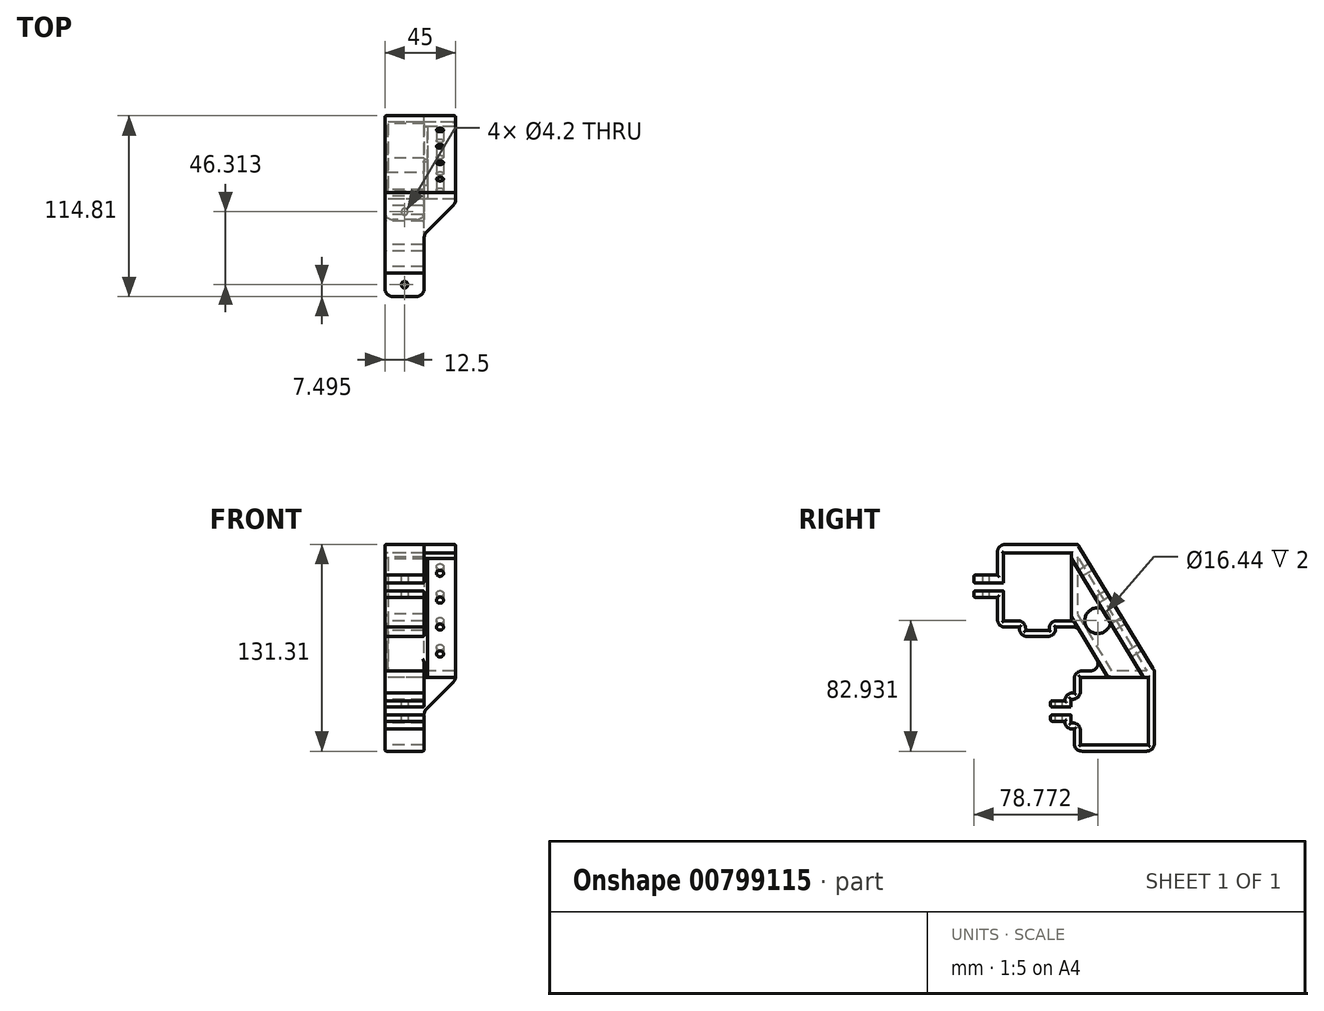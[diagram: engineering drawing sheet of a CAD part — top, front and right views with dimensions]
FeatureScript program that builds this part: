
annotation { "Feature Type Name" : "Feature", "Feature Type Description" : "" }
export const myFeature = defineFeature(function(context is Context, id is Id, definition is map)
    precondition{}
    {
        {
            var Q0;
            Q0=qCreatedBy(makeId("Right.planeOp"),FACE);
            var sketch = newSketch(context, id + "F0", { "sketchPlane" : qUnion([Q0])});
            skLineSegment(sketch, "E0.top", {"start": v(-257.11, -62.31) * mm, "end": v(-308.11, -62.31) * mm});
            skLineSegment(sketch, "E0.left", {"start": v(-257.11, -16.31) * mm, "end": v(-257.11, -62.31) * mm});
            skLineSegment(sketch, "E1.bottom", {"start": v(-304.11, -58.31) * mm, "end": v(-261.11, -58.31) * mm});
            skLineSegment(sketch, "E1.top", {"start": v(-304.11, -15.31) * mm, "end": v(-261.11, -15.31) * mm});
            skLineSegment(sketch, "E1.left", {"start": v(-304.11, -58.31) * mm, "end": v(-304.11, -44.31) * mm});
            skLineSegment(sketch, "E1.right", {"start": v(-261.11, -58.31) * mm, "end": v(-261.11, -15.31) * mm});
            skLineSegment(sketch, "E2.top", {"start": v(-323.11, -34.31) * mm, "end": v(-310.11, -34.31) * mm});
            skLineSegment(sketch, "E3.trimOffspring", {"start": v(-304.11, -29.31) * mm, "end": v(-304.11, -15.31) * mm});
            skLineSegment(sketch, "E4", {"start": v(-257.11, -11.31) * mm, "end": v(-308.11, -11.31) * mm});
            skLineSegment(sketch, "E5", {"start": v(-257.11, -16.31) * mm, "end": v(-257.11, -11.31) * mm});
            skLineSegment(sketch, "E6.top", {"start": v(-305.92, 16.5) * mm, "end": v(-323.92, 16.5) * mm});
            skLineSegment(sketch, "E6.left", {"start": v(-305.92, 64) * mm, "end": v(-305.92, 16.5) * mm});
            skLineSegment(sketch, "E7.bottom", {"start": v(-352.92, 20.5) * mm, "end": v(-338.92, 20.5) * mm});
            skLineSegment(sketch, "E7.top", {"start": v(-352.92, 63.5) * mm, "end": v(-309.92, 63.5) * mm});
            skLineSegment(sketch, "E7.left", {"start": v(-352.92, 20.5) * mm, "end": v(-352.92, 39.45) * mm});
            skLineSegment(sketch, "E7.right", {"start": v(-309.92, 20.5) * mm, "end": v(-309.92, 63.5) * mm});
            skLineSegment(sketch, "E8.top", {"start": v(-371.92, 44.5) * mm, "end": v(-352.92, 44.5) * mm});
            skLineSegment(sketch, "E9.trimOffspring", {"start": v(-352.92, 44.5) * mm, "end": v(-352.92, 63.5) * mm});
            skLineSegment(sketch, "E10", {"start": v(-356.92, 49.5) * mm, "end": v(-371.92, 49.5) * mm});
            skLineSegment(sketch, "E11", {"start": v(-371.92, 49.5) * mm, "end": v(-371.92, 44.5) * mm});
            skLineSegment(sketch, "E12", {"start": v(-305.92, 69) * mm, "end": v(-356.92, 69) * mm});
            skLineSegment(sketch, "E13", {"start": v(-305.92, 64) * mm, "end": v(-305.92, 69) * mm});
            skLineSegment(sketch, "E14", {"start": v(-305.92, 69) * mm, "end": v(-257.11, -11.31) * mm});
            skLineSegment(sketch, "E15", {"start": v(-305.92, 16.5) * mm, "end": v(-289.02, -11.31) * mm});
            skLineSegment(sketch, "E16", {"start": v(-266.47, -11.31) * mm, "end": v(-305.92, 53.6) * mm});
            skLineSegment(sketch, "E17", {"start": v(-289.02, -11.31) * mm, "end": v(-284.02, -11.31) * mm});
            skLineSegment(sketch, "E18", {"start": v(-284.02, -11.31) * mm, "end": v(-305.92, 24.73) * mm});
            skLineSegment(sketch, "E19", {"start": v(-276.96, 21.34) * mm, "end": v(-283.8, 17.19) * mm, "construction": true});
            skLineSegment(sketch, "E20", {"start": v(-309.92, 42) * mm, "end": v(-305.92, 42) * mm, "construction": true});
            skLineSegment(sketch, "E21", {"start": v(-261.11, -36.81) * mm, "end": v(-257.11, -36.81) * mm, "construction": true});
            skLineSegment(sketch, "E22", {"start": v(-331.42, 20.5) * mm, "end": v(-331.42, 16.5) * mm, "construction": true});
            skLineSegment(sketch, "E23", {"start": v(-332.38, 69) * mm, "end": v(-332.38, 63.5) * mm, "construction": true});
            skLineSegment(sketch, "E24", {"start": v(-356.92, 35.96) * mm, "end": v(-352.92, 35.96) * mm, "construction": true});
            skLineSegment(sketch, "E25", {"start": v(-356.92, 35.96) * mm, "end": v(-356.92, 16.5) * mm});
            skLineSegment(sketch, "E26", {"start": v(-352.92, 63.5) * mm, "end": v(-356.92, 63.5) * mm, "construction": true});
            skLineSegment(sketch, "E27", {"start": v(-356.92, 69) * mm, "end": v(-356.92, 49.5) * mm});
            skPoint(sketch, "E28.orphan", {"position": v(-358.83, 69) * mm});
            skLineSegment(sketch, "E29", {"start": v(-352.92, 39.45) * mm, "end": v(-371.92, 39.45) * mm});
            skLineSegment(sketch, "E30", {"start": v(-371.92, 39.45) * mm, "end": v(-371.92, 35.45) * mm});
            skLineSegment(sketch, "E31", {"start": v(-371.92, 35.45) * mm, "end": v(-356.92, 35.45) * mm});
            skLineSegment(sketch, "E32", {"start": v(-280.09, -58.31) * mm, "end": v(-280.09, -62.31) * mm, "construction": true});
            skLineSegment(sketch, "E33", {"start": v(-282.61, -15.31) * mm, "end": v(-282.61, -11.31) * mm, "construction": true});
            skLineSegment(sketch, "E34", {"start": v(-304.11, -15.31) * mm, "end": v(-308.11, -15.31) * mm, "construction": true});
            skLineSegment(sketch, "E35", {"start": v(-323.11, -34.31) * mm, "end": v(-323.11, -30.31) * mm});
            skLineSegment(sketch, "E36", {"start": v(-310.11, -30.31) * mm, "end": v(-323.11, -30.31) * mm});
            skLineSegment(sketch, "E37", {"start": v(-308.11, -25.31) * mm, "end": v(-308.11, -11.31) * mm});
            skLineSegment(sketch, "E38", {"start": v(-310.11, -39.31) * mm, "end": v(-323.11, -39.31) * mm});
            skLineSegment(sketch, "E39", {"start": v(-323.11, -39.31) * mm, "end": v(-323.11, -43.31) * mm});
            skLineSegment(sketch, "E40", {"start": v(-323.11, -43.31) * mm, "end": v(-310.11, -43.31) * mm});
            skLineSegment(sketch, "E41", {"start": v(-308.11, -48.31) * mm, "end": v(-308.11, -62.31) * mm});
            skLineSegment(sketch, "E42.bottom", {"start": v(-338.92, 14.5) * mm, "end": v(-323.92, 14.5) * mm});
            skLineSegment(sketch, "E42.left", {"start": v(-338.92, 14.5) * mm, "end": v(-338.92, 20.5) * mm});
            skLineSegment(sketch, "E42.right", {"start": v(-323.92, 14.5) * mm, "end": v(-323.92, 20.5) * mm});
            skPoint(sketch, "E42.middle", {"position": v(-331.42, 20.5) * mm});
            skLineSegment(sketch, "E43", {"start": v(-331.42, 14.5) * mm, "end": v(-331.42, 10.5) * mm, "construction": true});
            skLineSegment(sketch, "E44", {"start": v(-323.92, 15.67) * mm, "end": v(-319.92, 15.67) * mm, "construction": true});
            skLineSegment(sketch, "E45", {"start": v(-319.92, 16.5) * mm, "end": v(-319.92, 10.5) * mm});
            skLineSegment(sketch, "E46", {"start": v(-319.92, 10.5) * mm, "end": v(-331.42, 10.5) * mm});
            skLineSegment(sketch, "E47.MirrorCS", {"start": v(-342.92, 10.5) * mm, "end": v(-331.42, 10.5) * mm});
            skLineSegment(sketch, "E48.MirrorCS", {"start": v(-342.92, 16.5) * mm, "end": v(-342.92, 10.5) * mm});
            skPoint(sketch, "E49.orphan", {"position": v(-323.92, 26.5) * mm});
            skPoint(sketch, "E50.orphan", {"position": v(-338.92, 26.5) * mm});
            skLineSegment(sketch, "E51.trimOffspring", {"start": v(-323.92, 20.5) * mm, "end": v(-309.92, 20.5) * mm});
            skLineSegment(sketch, "E52.trimOffspring", {"start": v(-338.92, 16.5) * mm, "end": v(-356.92, 16.5) * mm});
            skLineSegment(sketch, "E53", {"start": v(-304.11, -34.31) * mm, "end": v(-304.11, -39.31) * mm, "construction": true});
            skLineSegment(sketch, "E54.bottom", {"start": v(-310.11, -44.31) * mm, "end": v(-304.11, -44.31) * mm});
            skLineSegment(sketch, "E54.top", {"start": v(-310.11, -29.31) * mm, "end": v(-304.11, -29.31) * mm});
            skLineSegment(sketch, "E54.left", {"start": v(-310.11, -44.31) * mm, "end": v(-310.11, -39.31) * mm});
            skPoint(sketch, "E54.middle", {"position": v(-304.11, -36.81) * mm});
            skLineSegment(sketch, "E55", {"start": v(-310.11, -29.31) * mm, "end": v(-310.11, -25.31) * mm, "construction": true});
            skLineSegment(sketch, "E56", {"start": v(-310.11, -29.31) * mm, "end": v(-314.11, -29.31) * mm, "construction": true});
            skLineSegment(sketch, "E57", {"start": v(-308.11, -25.31) * mm, "end": v(-314.11, -25.31) * mm});
            skLineSegment(sketch, "E58", {"start": v(-314.11, -25.31) * mm, "end": v(-314.11, -30.31) * mm});
            skLineSegment(sketch, "E59", {"start": v(-304.11, -36.81) * mm, "end": v(-328.83, -36.81) * mm, "construction": true});
            skLineSegment(sketch, "E60.MirrorCS", {"start": v(-314.11, -48.31) * mm, "end": v(-314.11, -43.31) * mm});
            skLineSegment(sketch, "E61.MirrorCS", {"start": v(-308.11, -48.31) * mm, "end": v(-314.11, -48.31) * mm});
            skLineSegment(sketch, "E62.trimOffspring", {"start": v(-310.11, -34.31) * mm, "end": v(-310.11, -29.31) * mm});
            skPoint(sketch, "E63.orphan", {"position": v(-298.11, -29.31) * mm});
            skPoint(sketch, "E64.orphan", {"position": v(-298.11, -44.31) * mm});
            skPoint(sketch, "E65.orphan", {"position": v(-308.11, -30.31) * mm});
            skPoint(sketch, "E66.orphan", {"position": v(-308.11, -43.31) * mm});
            skSolve(sketch);
        }
        {
            var Q0;
            Q0=qSketchRegion(id+"F0",true);
            extrude(context, id + "F1", {"entities" : qUnion([Q0]), "depth" : 25 * mm, "offsetDistance" : 25 * mm});
        }
        {
            var Q0;
            Q0=makeQuery(id+"F1.opExtrude","CAP_FACE",FACE,{"disambiguationData":[OSD([sQuery(id+"F0.wireOp",EDGE,"E0.top"),sQuery(id+"F0.wireOp",EDGE,"E0.left"),sQuery(id+"F0.wireOp",EDGE,"E1.bottom"),sQuery(id+"F0.wireOp",EDGE,"E1.top"),sQuery(id+"F0.wireOp",EDGE,"E1.left"),sQuery(id+"F0.wireOp",EDGE,"E1.right"),sQuery(id+"F0.wireOp",EDGE,"E2.bottom"),sQuery(id+"F0.wireOp",EDGE,"E2.top"),sQuery(id+"F0.wireOp",EDGE,"E3.trimOffspring"),sQuery(id+"F0.wireOp",EDGE,"97N35CGi-qyRt-fTuY-865t-gSXGTTs39KFh"),sQuery(id+"F0.wireOp",EDGE,"YVl5jyTW-9yZZ-gB00-PbPT-4uCPtmQBn0Fz"),sQuery(id+"F0.wireOp",EDGE,"DkqYmhQx-Zx2j-OynX-PNvr-HeUXXOLSZVF7"),sQuery(id+"F0.wireOp",EDGE,"8b463ff5-7117-4e72-8e2d-57af3a9758190.MirrorCS"),sQuery(id+"F0.wireOp",EDGE,"a2a913a1-f987-4361-a245-a8682805a7f70.MirrorCS"),sQuery(id+"F0.wireOp",EDGE,"813ea5ba-1d3b-4507-9dff-333e66d3a4c90.MirrorCS"),sQuery(id+"F0.wireOp",EDGE,"E4"),sQuery(id+"F0.wireOp",EDGE,"E5"),sQuery(id+"F0.wireOp",EDGE,"E6.top"),sQuery(id+"F0.wireOp",EDGE,"E6.left"),sQuery(id+"F0.wireOp",EDGE,"E7.bottom"),sQuery(id+"F0.wireOp",EDGE,"E7.top"),sQuery(id+"F0.wireOp",EDGE,"E7.left"),sQuery(id+"F0.wireOp",EDGE,"E7.right"),sQuery(id+"F0.wireOp",EDGE,"E8.bottom"),sQuery(id+"F0.wireOp",EDGE,"E8.top"),sQuery(id+"F0.wireOp",EDGE,"E9.trimOffspring"),sQuery(id+"F0.wireOp",EDGE,"463e9aad-9224-478d-ada1-befd63aa6510"),sQuery(id+"F0.wireOp",EDGE,"E10"),sQuery(id+"F0.wireOp",EDGE,"E11"),sQuery(id+"F0.wireOp",EDGE,"d85e5b7c-68ab-4a60-b65d-d2910f881e3b.MirrorCS"),sQuery(id+"F0.wireOp",EDGE,"648d8bc0-cce0-4394-85f9-bea9f80b14ba.MirrorCS"),sQuery(id+"F0.wireOp",EDGE,"03109c16-8484-40c6-ad21-c417801123f2.MirrorCS"),sQuery(id+"F0.wireOp",EDGE,"E12"),sQuery(id+"F0.wireOp",EDGE,"E14"),sQuery(id+"F0.wireOp",EDGE,"E15"),sQuery(id+"F0.wireOp",EDGE,"E16"),sQuery(id+"F0.wireOp",EDGE,"E18")])],"isStart":false});
            var sketch = newSketch(context, id + "F2", { "sketchPlane" : qUnion([Q0])});
            skLineSegment(sketch, "E67", {"start": v(-305.92, 69) * mm, "end": v(-257.11, -11.31) * mm});
            skLineSegment(sketch, "E68", {"start": v(-305.92, 53.6) * mm, "end": v(-263.95, -15.47) * mm});
            skLineSegment(sketch, "E69", {"start": v(-257.11, -11.31) * mm, "end": v(-263.95, -15.47) * mm});
            skLineSegment(sketch, "E70", {"start": v(-305.92, 69) * mm, "end": v(-312.76, 64.84) * mm});
            skLineSegment(sketch, "E71", {"start": v(-305.92, 53.6) * mm, "end": v(-313.8, 66.57) * mm});
            skLineSegment(sketch, "E72", {"start": v(-312.76, 64.84) * mm, "end": v(-313.8, 66.57) * mm});
            skPoint(sketch, "E73.orphan", {"position": v(-309.92, 66.57) * mm});
            skSolve(sketch);
        }
        {
            var Q0;
            Q0=qSketchRegion(id+"F2",true);
            extrude(context, id + "F3", {"entities" : qUnion([Q0]), "operationType" : NewBodyOperationType.ADD, "depth" : 20 * mm, "offsetDistance" : 25 * mm});
        }
        {
            var Q0;
            Q0=makeQuery(id+"F1.opExtrude","SWEPT_FACE",FACE,{"disambiguationData":[OSD([sQuery(id+"F0.wireOp",EDGE,"E40")])]});
            var sketch = newSketch(context, id + "F4", { "sketchPlane" : qUnion([Q0])});
            skCircle(sketch, "E74", {"center": v(12.5, 318.11) * mm, "radius": 2.1 * mm});
            skLineSegment(sketch, "E75", {"start": v(12.5, 318.11) * mm, "end": v(12.5, 323.11) * mm, "construction": true});
            skSolve(sketch);
        }
        {
            var Q0;
            Q0=qSketchRegion(id+"F4",true);
            extrude(context, id + "F5", {"entities" : qUnion([Q0]), "operationType" : NewBodyOperationType.REMOVE, "oppositeDirection" : true, "depth" : 25 * mm, "offsetDistance" : 25 * mm});
        }
        {
            var Q0;
            Q0=makeQuery(id+"F1.opExtrude","SWEPT_FACE",FACE,{"disambiguationData":[OSD([sQuery(id+"F0.wireOp",EDGE,"E31")])]});
            var sketch = newSketch(context, id + "F6", { "sketchPlane" : qUnion([Q0])});
            skLineSegment(sketch, "E76", {"start": v(0, 364.42) * mm, "end": v(25, 364.42) * mm, "construction": true});
            skCircle(sketch, "E77", {"center": v(12.5, 364.42) * mm, "radius": 2.1 * mm});
            skSolve(sketch);
        }
        {
            var Q0;
            Q0=qSketchRegion(id+"F6",true);
            extrude(context, id + "F7", {"entities" : qUnion([Q0]), "operationType" : NewBodyOperationType.REMOVE, "oppositeDirection" : true, "depth" : 25 * mm, "offsetDistance" : 25 * mm});
        }
        {
            var Q0;
            Q0=makeQuery(id+"F3.boolean.opBoolean","MERGE",FACE,{"derivedFrom":[makeQuery(id+"F1.opExtrude","SWEPT_FACE",FACE,{"disambiguationData":[OSD([sQuery(id+"F0.wireOp",EDGE,"E16")])]}),makeQuery(id+"F3.opExtrude","SWEPT_FACE",FACE,{"disambiguationData":[OSD([sQuery(id+"F2.wireOp",EDGE,"E68"),sQuery(id+"F2.wireOp",EDGE,"E71")])]})]});
            var sketch = newSketch(context, id + "F8", { "sketchPlane" : qUnion([Q0])});
            skLineSegment(sketch, "E78", {"start": v(35, 124.76) * mm, "end": v(35, 217.85) * mm, "construction": true});
            skPoint(sketch, "E78.startSnap0", {"position": v(35, 123.87) * mm});
            skLineSegment(sketch, "E79", {"start": v(35, 171.3) * mm, "end": v(25.9, 171.3) * mm, "construction": true});
            skLineSegment(sketch, "E80", {"start": v(25.9, 171.3) * mm, "end": v(45, 171.3) * mm, "construction": true});
            skLineSegment(sketch, "E81", {"start": v(35, 171.3) * mm, "end": v(35, 181.3) * mm, "construction": true});
            skLineSegment(sketch, "E82", {"start": v(35, 181.3) * mm, "end": v(35, 201.3) * mm, "construction": true});
            skCircle(sketch, "E83", {"center": v(35, 181.3) * mm, "radius": 2.25 * mm});
            skCircle(sketch, "E84", {"center": v(35, 201.3) * mm, "radius": 2.25 * mm});
            skCircle(sketch, "E85.MirrorC", {"center": v(35, 161.3) * mm, "radius": 2.25 * mm});
            skCircle(sketch, "E86.MirrorC", {"center": v(35, 141.3) * mm, "radius": 2.25 * mm});
            skSolve(sketch);
        }
        {
            var Q0;
            Q0=qSketchRegion(id+"F8",true);
            extrude(context, id + "F9", {"entities" : qUnion([Q0]), "operationType" : NewBodyOperationType.REMOVE, "oppositeDirection" : true, "depth" : 25 * mm, "offsetDistance" : 25 * mm});
        }
        {
            var Q0;
            {var subQ0=sQuery(id+"F0.wireOp",EDGE,"E27");var subQ5=sQuery(id+"F0.wireOp",EDGE,"E16");var subQ6=sQuery(id+"F0.wireOp",EDGE,"E14");var subQ7=sQuery(id+"F0.wireOp",EDGE,"E12");var subQ8=sQuery(id+"F0.wireOp",EDGE,"E11");var subQ9=sQuery(id+"F0.wireOp",EDGE,"E7.top");var subQ10=sQuery(id+"F0.wireOp",EDGE,"E10");var subQ11=sQuery(id+"F0.wireOp",EDGE,"E8.top");var subQ12=sQuery(id+"F0.wireOp",EDGE,"E9.trimOffspring");Q0=makeQuery(id+"F3.boolean.opBoolean","SPLIT",FACE,{"disambiguationData":[TD([makeQuery(id+"F1.opExtrude","SWEPT_FACE",FACE,{"disambiguationData":[OSD([subQ9])]})])],"derivedFrom":makeQuery(id+"F1.opExtrude","CAP_FACE",FACE,{"disambiguationData":[OSD([sQuery(id+"F0.wireOp",EDGE,"E0.top"),sQuery(id+"F0.wireOp",EDGE,"E0.left"),sQuery(id+"F0.wireOp",EDGE,"E1.bottom"),sQuery(id+"F0.wireOp",EDGE,"E1.top"),sQuery(id+"F0.wireOp",EDGE,"E1.left"),sQuery(id+"F0.wireOp",EDGE,"E1.right"),sQuery(id+"F0.wireOp",EDGE,"E2.top"),sQuery(id+"F0.wireOp",EDGE,"E3.trimOffspring"),sQuery(id+"F0.wireOp",EDGE,"E4"),sQuery(id+"F0.wireOp",EDGE,"E5"),sQuery(id+"F0.wireOp",EDGE,"E6.top"),sQuery(id+"F0.wireOp",EDGE,"E6.left"),sQuery(id+"F0.wireOp",EDGE,"E7.bottom"),subQ9,sQuery(id+"F0.wireOp",EDGE,"E7.left"),sQuery(id+"F0.wireOp",EDGE,"E7.right"),subQ11,subQ12,subQ10,subQ8,subQ7,subQ6,sQuery(id+"F0.wireOp",EDGE,"E15"),subQ5,sQuery(id+"F0.wireOp",EDGE,"E18"),sQuery(id+"F0.wireOp",EDGE,"E25"),subQ0,sQuery(id+"F0.wireOp",EDGE,"E29"),sQuery(id+"F0.wireOp",EDGE,"E30"),sQuery(id+"F0.wireOp",EDGE,"E31"),sQuery(id+"F0.wireOp",EDGE,"E35"),sQuery(id+"F0.wireOp",EDGE,"E36"),sQuery(id+"F0.wireOp",EDGE,"E37"),sQuery(id+"F0.wireOp",EDGE,"E38"),sQuery(id+"F0.wireOp",EDGE,"E39"),sQuery(id+"F0.wireOp",EDGE,"E40"),sQuery(id+"F0.wireOp",EDGE,"E41"),sQuery(id+"F0.wireOp",EDGE,"E42.bottom"),sQuery(id+"F0.wireOp",EDGE,"E42.left"),sQuery(id+"F0.wireOp",EDGE,"E42.right"),sQuery(id+"F0.wireOp",EDGE,"E45"),sQuery(id+"F0.wireOp",EDGE,"E46"),sQuery(id+"F0.wireOp",EDGE,"E47.MirrorCS"),sQuery(id+"F0.wireOp",EDGE,"E48.MirrorCS"),sQuery(id+"F0.wireOp",EDGE,"E51.trimOffspring"),sQuery(id+"F0.wireOp",EDGE,"E52.trimOffspring"),sQuery(id+"F0.wireOp",EDGE,"E54.bottom"),sQuery(id+"F0.wireOp",EDGE,"E54.top"),sQuery(id+"F0.wireOp",EDGE,"E54.left"),sQuery(id+"F0.wireOp",EDGE,"E57"),sQuery(id+"F0.wireOp",EDGE,"E58"),sQuery(id+"F0.wireOp",EDGE,"E60.MirrorCS"),sQuery(id+"F0.wireOp",EDGE,"E61.MirrorCS"),sQuery(id+"F0.wireOp",EDGE,"E62.trimOffspring")])],"isStart":false})});}
            var sketch = newSketch(context, id + "F10", { "sketchPlane" : qUnion([Q0])});
            skLineSegment(sketch, "E87.bottom", {"start": v(-284.02, -11.31) * mm, "end": v(-284.02, -11.31) * mm});
            skLineSegment(sketch, "E87.top", {"start": v(-284.02, -15.31) * mm, "end": v(-284.02, -15.31) * mm});
            skLineSegment(sketch, "E87.left", {"start": v(-284.02, -11.31) * mm, "end": v(-284.02, -15.31) * mm});
            skLineSegment(sketch, "E87.right", {"start": v(-284.02, -11.31) * mm, "end": v(-284.02, -15.31) * mm});
            skLineSegment(sketch, "E88.bottom", {"start": v(-332.43, 63.5) * mm, "end": v(-305.92, 63.5) * mm});
            skLineSegment(sketch, "E88.top", {"start": v(-332.43, 69) * mm, "end": v(-305.92, 69) * mm});
            skLineSegment(sketch, "E88.left", {"start": v(-332.43, 63.5) * mm, "end": v(-332.43, 69) * mm});
            skLineSegment(sketch, "E88.right", {"start": v(-305.92, 63.5) * mm, "end": v(-305.92, 69) * mm});
            skSolve(sketch);
        }
        {
            var Q0;
            Q0=qSketchRegion(id+"F10",true);
            extrude(context, id + "F11", {"entities" : qUnion([Q0]), "operationType" : NewBodyOperationType.ADD, "depth" : 20 * mm, "offsetDistance" : 25 * mm});
        }
        {
            var Q0;
            {var subQ0=sQuery(id+"F0.wireOp",EDGE,"E38");var subQ1=sQuery(id+"F0.wireOp",EDGE,"E14");var subQ2=sQuery(id+"F0.wireOp",EDGE,"E0.top");var subQ3=sQuery(id+"F0.wireOp",EDGE,"E1.right");var subQ4=sQuery(id+"F0.wireOp",EDGE,"E61.MirrorCS");var subQ5=sQuery(id+"F0.wireOp",EDGE,"E1.left");var subQ6=sQuery(id+"F0.wireOp",EDGE,"E60.MirrorCS");var subQ7=sQuery(id+"F0.wireOp",EDGE,"E1.top");var subQ10=sQuery(id+"F0.wireOp",EDGE,"E39");var subQ11=sQuery(id+"F0.wireOp",EDGE,"E5");var subQ12=sQuery(id+"F0.wireOp",EDGE,"E0.left");var subQ13=sQuery(id+"F0.wireOp",EDGE,"E54.left");var subQ14=sQuery(id+"F0.wireOp",EDGE,"E40");var subQ15=sQuery(id+"F0.wireOp",EDGE,"E1.bottom");var subQ16=sQuery(id+"F0.wireOp",EDGE,"E41");var subQ17=sQuery(id+"F0.wireOp",EDGE,"E54.bottom");Q0=makeQuery(id+"F3.boolean.opBoolean","SPLIT",FACE,{"disambiguationData":[TD([makeQuery(id+"F1.opExtrude","SWEPT_FACE",FACE,{"disambiguationData":[OSD([subQ2])]})])],"derivedFrom":makeQuery(id+"F1.opExtrude","CAP_FACE",FACE,{"disambiguationData":[OSD([subQ2,subQ12,subQ15,subQ7,subQ5,subQ3,sQuery(id+"F0.wireOp",EDGE,"E2.top"),sQuery(id+"F0.wireOp",EDGE,"E3.trimOffspring"),sQuery(id+"F0.wireOp",EDGE,"E4"),subQ11,sQuery(id+"F0.wireOp",EDGE,"E6.top"),sQuery(id+"F0.wireOp",EDGE,"E6.left"),sQuery(id+"F0.wireOp",EDGE,"E7.bottom"),sQuery(id+"F0.wireOp",EDGE,"E7.top"),sQuery(id+"F0.wireOp",EDGE,"E7.left"),sQuery(id+"F0.wireOp",EDGE,"E7.right"),sQuery(id+"F0.wireOp",EDGE,"E8.top"),sQuery(id+"F0.wireOp",EDGE,"E9.trimOffspring"),sQuery(id+"F0.wireOp",EDGE,"E10"),sQuery(id+"F0.wireOp",EDGE,"E11"),sQuery(id+"F0.wireOp",EDGE,"E12"),subQ1,sQuery(id+"F0.wireOp",EDGE,"E15"),sQuery(id+"F0.wireOp",EDGE,"E16"),sQuery(id+"F0.wireOp",EDGE,"E18"),sQuery(id+"F0.wireOp",EDGE,"E25"),sQuery(id+"F0.wireOp",EDGE,"E27"),sQuery(id+"F0.wireOp",EDGE,"E29"),sQuery(id+"F0.wireOp",EDGE,"E30"),sQuery(id+"F0.wireOp",EDGE,"E31"),sQuery(id+"F0.wireOp",EDGE,"E35"),sQuery(id+"F0.wireOp",EDGE,"E36"),sQuery(id+"F0.wireOp",EDGE,"E37"),subQ0,subQ10,subQ14,subQ16,sQuery(id+"F0.wireOp",EDGE,"E42.bottom"),sQuery(id+"F0.wireOp",EDGE,"E42.left"),sQuery(id+"F0.wireOp",EDGE,"E42.right"),sQuery(id+"F0.wireOp",EDGE,"E45"),sQuery(id+"F0.wireOp",EDGE,"E46"),sQuery(id+"F0.wireOp",EDGE,"E47.MirrorCS"),sQuery(id+"F0.wireOp",EDGE,"E48.MirrorCS"),sQuery(id+"F0.wireOp",EDGE,"E51.trimOffspring"),sQuery(id+"F0.wireOp",EDGE,"E52.trimOffspring"),subQ17,sQuery(id+"F0.wireOp",EDGE,"E54.top"),subQ13,sQuery(id+"F0.wireOp",EDGE,"E57"),sQuery(id+"F0.wireOp",EDGE,"E58"),subQ6,subQ4,sQuery(id+"F0.wireOp",EDGE,"E62.trimOffspring")])],"isStart":false})});}
            var sketch = newSketch(context, id + "F12", { "sketchPlane" : qUnion([Q0])});
            skLineSegment(sketch, "E89.bottom", {"start": v(-257.11, -36.81) * mm, "end": v(-261.11, -36.81) * mm});
            skLineSegment(sketch, "E89.top", {"start": v(-257.11, -11.31) * mm, "end": v(-261.11, -11.31) * mm});
            skLineSegment(sketch, "E89.left", {"start": v(-257.11, -36.81) * mm, "end": v(-257.11, -11.31) * mm});
            skLineSegment(sketch, "E89.right", {"start": v(-261.11, -36.81) * mm, "end": v(-261.11, -11.31) * mm});
            skSolve(sketch);
        }
        {
            var Q0;
            Q0=qSketchRegion(id+"F12",true);
            extrude(context, id + "F13", {"entities" : qUnion([Q0]), "operationType" : NewBodyOperationType.ADD, "depth" : 20 * mm, "offsetDistance" : 25 * mm});
        }
        {
            var Q0;
            {var subQ0=sQuery(id+"F0.wireOp",EDGE,"E30");var subQ1=sQuery(id+"F0.wireOp",EDGE,"E29");var subQ4=sQuery(id+"F0.wireOp",EDGE,"E25");var subQ5=sQuery(id+"F0.wireOp",EDGE,"E18");var subQ6=sQuery(id+"F0.wireOp",EDGE,"E16");var subQ7=sQuery(id+"F0.wireOp",EDGE,"E15");var subQ8=sQuery(id+"F0.wireOp",EDGE,"E35");var subQ9=sQuery(id+"F0.wireOp",EDGE,"E3.trimOffspring");var subQ10=sQuery(id+"F0.wireOp",EDGE,"E31");var subQ11=sQuery(id+"F0.wireOp",EDGE,"E2.top");var subQ12=sQuery(id+"F0.wireOp",EDGE,"E36");var subQ13=sQuery(id+"F0.wireOp",EDGE,"E4");var subQ15=sQuery(id+"F0.wireOp",EDGE,"E1.top");var subQ16=sQuery(id+"F0.wireOp",EDGE,"E42.bottom");var subQ17=sQuery(id+"F0.wireOp",EDGE,"E7.left");var subQ18=sQuery(id+"F0.wireOp",EDGE,"E37");var subQ19=sQuery(id+"F0.wireOp",EDGE,"E6.top");var subQ20=sQuery(id+"F0.wireOp",EDGE,"E6.left");var subQ21=sQuery(id+"F0.wireOp",EDGE,"E7.bottom");var subQ22=sQuery(id+"F0.wireOp",EDGE,"E42.left");var subQ23=sQuery(id+"F0.wireOp",EDGE,"E7.right");var subQ24=sQuery(id+"F0.wireOp",EDGE,"E42.right");var subQ25=sQuery(id+"F0.wireOp",EDGE,"E45");var subQ26=sQuery(id+"F0.wireOp",EDGE,"E47.MirrorCS");var subQ27=sQuery(id+"F0.wireOp",EDGE,"E46");var subQ28=sQuery(id+"F0.wireOp",EDGE,"E48.MirrorCS");var subQ29=sQuery(id+"F0.wireOp",EDGE,"E51.trimOffspring");var subQ30=sQuery(id+"F0.wireOp",EDGE,"E52.trimOffspring");var subQ31=sQuery(id+"F0.wireOp",EDGE,"E54.top");var subQ32=sQuery(id+"F0.wireOp",EDGE,"E57");var subQ33=sQuery(id+"F0.wireOp",EDGE,"E58");var subQ34=sQuery(id+"F0.wireOp",EDGE,"E62.trimOffspring");Q0=makeQuery(id+"F3.boolean.opBoolean","SPLIT",FACE,{"disambiguationData":[TD([makeQuery(id+"F1.opExtrude","SWEPT_FACE",FACE,{"disambiguationData":[OSD([subQ11])]})])],"derivedFrom":makeQuery(id+"F1.opExtrude","CAP_FACE",FACE,{"disambiguationData":[OSD([sQuery(id+"F0.wireOp",EDGE,"E0.top"),sQuery(id+"F0.wireOp",EDGE,"E0.left"),sQuery(id+"F0.wireOp",EDGE,"E1.bottom"),subQ15,sQuery(id+"F0.wireOp",EDGE,"E1.left"),sQuery(id+"F0.wireOp",EDGE,"E1.right"),subQ11,subQ9,subQ13,sQuery(id+"F0.wireOp",EDGE,"E5"),subQ19,subQ20,subQ21,sQuery(id+"F0.wireOp",EDGE,"E7.top"),subQ17,subQ23,sQuery(id+"F0.wireOp",EDGE,"E8.top"),sQuery(id+"F0.wireOp",EDGE,"E9.trimOffspring"),sQuery(id+"F0.wireOp",EDGE,"E10"),sQuery(id+"F0.wireOp",EDGE,"E11"),sQuery(id+"F0.wireOp",EDGE,"E12"),sQuery(id+"F0.wireOp",EDGE,"E14"),subQ7,subQ6,subQ5,subQ4,sQuery(id+"F0.wireOp",EDGE,"E27"),subQ1,subQ0,subQ10,subQ8,subQ12,subQ18,sQuery(id+"F0.wireOp",EDGE,"E38"),sQuery(id+"F0.wireOp",EDGE,"E39"),sQuery(id+"F0.wireOp",EDGE,"E40"),sQuery(id+"F0.wireOp",EDGE,"E41"),subQ16,subQ22,subQ24,subQ25,subQ27,subQ26,subQ28,subQ29,subQ30,sQuery(id+"F0.wireOp",EDGE,"E54.bottom"),subQ31,sQuery(id+"F0.wireOp",EDGE,"E54.left"),subQ32,subQ33,sQuery(id+"F0.wireOp",EDGE,"E60.MirrorCS"),sQuery(id+"F0.wireOp",EDGE,"E61.MirrorCS"),subQ34])],"isStart":false})});}
            var sketch = newSketch(context, id + "F14", { "sketchPlane" : qUnion([Q0])});
            skLineSegment(sketch, "E90.bottom", {"start": v(-264.04, -15.31) * mm, "end": v(-259.49, -15.31) * mm});
            skLineSegment(sketch, "E90.top", {"start": v(-264.04, -12.49) * mm, "end": v(-259.49, -12.49) * mm});
            skLineSegment(sketch, "E90.left", {"start": v(-264.04, -15.31) * mm, "end": v(-264.04, -12.49) * mm});
            skLineSegment(sketch, "E90.right", {"start": v(-259.49, -15.31) * mm, "end": v(-259.49, -12.49) * mm});
            skSolve(sketch);
        }
        {
            var Q0;
            Q0=qSketchRegion(id+"F14",true);
            extrude(context, id + "F15", {"entities" : qUnion([Q0]), "operationType" : NewBodyOperationType.ADD, "depth" : 20 * mm, "offsetDistance" : 25 * mm});
        }
        {
            var Q0;
            {var subQ1=sQuery(id+"F0.wireOp",EDGE,"E7.top");var subQ2=sQuery(id+"F2.wireOp",EDGE,"E71");var subQ3=sQuery(id+"F2.wireOp",EDGE,"E68");Q0=makeQuery(id+"F3.boolean.opBoolean","SPLIT",FACE,{"disambiguationData":[TD([makeQuery(id+"F1.opExtrude","SWEPT_FACE",FACE,{"disambiguationData":[OSD([subQ1])]})])],"derivedFrom":makeQuery(id+"F3.opExtrude","CAP_FACE",FACE,{"disambiguationData":[OSD([sQuery(id+"F2.wireOp",EDGE,"E67"),subQ3,sQuery(id+"F2.wireOp",EDGE,"E69"),sQuery(id+"F2.wireOp",EDGE,"E70"),subQ2])],"isStart":true})});}
            var sketch = newSketch(context, id + "F16", { "sketchPlane" : qUnion([Q0])});
            skLineSegment(sketch, "E91", {"start": v(309.92, 63.5) * mm, "end": v(309.92, 60.18) * mm});
            skLineSegment(sketch, "E92", {"start": v(309.92, 60.18) * mm, "end": v(311.94, 63.5) * mm});
            skLineSegment(sketch, "E93", {"start": v(311.94, 63.5) * mm, "end": v(309.92, 63.5) * mm});
            skSolve(sketch);
        }
        {
            var Q0;
            Q0=qSketchRegion(id+"F16",true);
            extrude(context, id + "F17", {"entities" : qUnion([Q0]), "operationType" : NewBodyOperationType.REMOVE, "oppositeDirection" : true, "depth" : 20 * mm, "offsetDistance" : 25 * mm});
        }
        {
            var Q0;
            Q0=makeQuery(id+"F13.opExtrude","CAP_EDGE",EDGE,{"disambiguationData":[OSD([sQuery(id+"F12.wireOp",EDGE,"E89.bottom")])],"isStart":false});
            var Q1;
            Q1=makeQuery(id+"F11.opExtrude","CAP_EDGE",EDGE,{"disambiguationData":[OSD([sQuery(id+"F10.wireOp",EDGE,"E88.left")])],"isStart":false});
            chamfer(context, id + "F18", {"entities" : qUnion([Q0, Q1]), "width" : 20 * mm, "tangentPropagation" : true});
        }
        {
            var Q0;
            {var subQ0=sQuery(id+"F0.wireOp",EDGE,"E30");var subQ1=sQuery(id+"F0.wireOp",EDGE,"E29");var subQ4=sQuery(id+"F0.wireOp",EDGE,"E25");var subQ5=sQuery(id+"F0.wireOp",EDGE,"E18");var subQ6=sQuery(id+"F0.wireOp",EDGE,"E16");var subQ7=sQuery(id+"F0.wireOp",EDGE,"E15");var subQ8=sQuery(id+"F0.wireOp",EDGE,"E35");var subQ9=sQuery(id+"F0.wireOp",EDGE,"E3.trimOffspring");var subQ10=sQuery(id+"F0.wireOp",EDGE,"E31");var subQ11=sQuery(id+"F0.wireOp",EDGE,"E2.top");var subQ12=sQuery(id+"F0.wireOp",EDGE,"E36");var subQ13=sQuery(id+"F0.wireOp",EDGE,"E4");var subQ15=sQuery(id+"F0.wireOp",EDGE,"E1.top");var subQ16=sQuery(id+"F0.wireOp",EDGE,"E42.bottom");var subQ17=sQuery(id+"F0.wireOp",EDGE,"E7.left");var subQ18=sQuery(id+"F0.wireOp",EDGE,"E37");var subQ19=sQuery(id+"F0.wireOp",EDGE,"E6.top");var subQ20=sQuery(id+"F0.wireOp",EDGE,"E6.left");var subQ21=sQuery(id+"F0.wireOp",EDGE,"E7.bottom");var subQ22=sQuery(id+"F0.wireOp",EDGE,"E42.left");var subQ23=sQuery(id+"F0.wireOp",EDGE,"E7.right");var subQ24=sQuery(id+"F0.wireOp",EDGE,"E42.right");var subQ25=sQuery(id+"F0.wireOp",EDGE,"E45");var subQ26=sQuery(id+"F0.wireOp",EDGE,"E47.MirrorCS");var subQ27=sQuery(id+"F0.wireOp",EDGE,"E46");var subQ28=sQuery(id+"F0.wireOp",EDGE,"E48.MirrorCS");var subQ29=sQuery(id+"F0.wireOp",EDGE,"E51.trimOffspring");var subQ30=sQuery(id+"F0.wireOp",EDGE,"E52.trimOffspring");var subQ31=sQuery(id+"F0.wireOp",EDGE,"E54.top");var subQ32=sQuery(id+"F0.wireOp",EDGE,"E57");var subQ33=sQuery(id+"F0.wireOp",EDGE,"E58");var subQ34=sQuery(id+"F0.wireOp",EDGE,"E62.trimOffspring");Q0=makeQuery(id+"F3.boolean.opBoolean","SPLIT",FACE,{"disambiguationData":[TD([makeQuery(id+"F1.opExtrude","SWEPT_FACE",FACE,{"disambiguationData":[OSD([subQ11])]})])],"derivedFrom":makeQuery(id+"F1.opExtrude","CAP_FACE",FACE,{"disambiguationData":[OSD([sQuery(id+"F0.wireOp",EDGE,"E0.top"),sQuery(id+"F0.wireOp",EDGE,"E0.left"),sQuery(id+"F0.wireOp",EDGE,"E1.bottom"),subQ15,sQuery(id+"F0.wireOp",EDGE,"E1.left"),sQuery(id+"F0.wireOp",EDGE,"E1.right"),subQ11,subQ9,subQ13,sQuery(id+"F0.wireOp",EDGE,"E5"),subQ19,subQ20,subQ21,sQuery(id+"F0.wireOp",EDGE,"E7.top"),subQ17,subQ23,sQuery(id+"F0.wireOp",EDGE,"E8.top"),sQuery(id+"F0.wireOp",EDGE,"E9.trimOffspring"),sQuery(id+"F0.wireOp",EDGE,"E10"),sQuery(id+"F0.wireOp",EDGE,"E11"),sQuery(id+"F0.wireOp",EDGE,"E12"),sQuery(id+"F0.wireOp",EDGE,"E14"),subQ7,subQ6,subQ5,subQ4,sQuery(id+"F0.wireOp",EDGE,"E27"),subQ1,subQ0,subQ10,subQ8,subQ12,subQ18,sQuery(id+"F0.wireOp",EDGE,"E38"),sQuery(id+"F0.wireOp",EDGE,"E39"),sQuery(id+"F0.wireOp",EDGE,"E40"),sQuery(id+"F0.wireOp",EDGE,"E41"),subQ16,subQ22,subQ24,subQ25,subQ27,subQ26,subQ28,subQ29,subQ30,sQuery(id+"F0.wireOp",EDGE,"E54.bottom"),subQ31,sQuery(id+"F0.wireOp",EDGE,"E54.left"),subQ32,subQ33,sQuery(id+"F0.wireOp",EDGE,"E60.MirrorCS"),sQuery(id+"F0.wireOp",EDGE,"E61.MirrorCS"),subQ34])],"isStart":false})});}
            var sketch = newSketch(context, id + "F19", { "sketchPlane" : qUnion([Q0])});
            skLineSegment(sketch, "E94", {"start": v(-264.04, -15.31) * mm, "end": v(-309.92, 60.18) * mm});
            skLineSegment(sketch, "E95", {"start": v(-289.02, -11.31) * mm, "end": v(-309.92, 23.08) * mm});
            skLineSegment(sketch, "E96", {"start": v(-309.92, 23.08) * mm, "end": v(-309.92, 60.18) * mm});
            skLineSegment(sketch, "E97", {"start": v(-289.02, -11.31) * mm, "end": v(-286.59, -15.31) * mm});
            skLineSegment(sketch, "E98", {"start": v(-286.59, -15.31) * mm, "end": v(-264.04, -15.31) * mm});
            skSolve(sketch);
        }
        {
            var Q0;
            Q0=qSketchRegion(id+"F19",true);
            extrude(context, id + "F20", {"entities" : qUnion([Q0]), "operationType" : NewBodyOperationType.ADD, "depth" : 2 * mm, "offsetDistance" : 25 * mm});
        }
        {
            var Q0;
            Q0=makeQuery(id+"F1.opExtrude","CAP_FACE",FACE,{"disambiguationData":[OSD([sQuery(id+"F0.wireOp",EDGE,"E0.top"),sQuery(id+"F0.wireOp",EDGE,"E0.left"),sQuery(id+"F0.wireOp",EDGE,"E1.bottom"),sQuery(id+"F0.wireOp",EDGE,"E1.top"),sQuery(id+"F0.wireOp",EDGE,"E1.left"),sQuery(id+"F0.wireOp",EDGE,"E1.right"),sQuery(id+"F0.wireOp",EDGE,"E2.top"),sQuery(id+"F0.wireOp",EDGE,"E3.trimOffspring"),sQuery(id+"F0.wireOp",EDGE,"E4"),sQuery(id+"F0.wireOp",EDGE,"E5"),sQuery(id+"F0.wireOp",EDGE,"E6.top"),sQuery(id+"F0.wireOp",EDGE,"E6.left"),sQuery(id+"F0.wireOp",EDGE,"E7.bottom"),sQuery(id+"F0.wireOp",EDGE,"E7.top"),sQuery(id+"F0.wireOp",EDGE,"E7.left"),sQuery(id+"F0.wireOp",EDGE,"E7.right"),sQuery(id+"F0.wireOp",EDGE,"E8.top"),sQuery(id+"F0.wireOp",EDGE,"E9.trimOffspring"),sQuery(id+"F0.wireOp",EDGE,"E10"),sQuery(id+"F0.wireOp",EDGE,"E11"),sQuery(id+"F0.wireOp",EDGE,"E12"),sQuery(id+"F0.wireOp",EDGE,"E14"),sQuery(id+"F0.wireOp",EDGE,"E15"),sQuery(id+"F0.wireOp",EDGE,"E16"),sQuery(id+"F0.wireOp",EDGE,"E18"),sQuery(id+"F0.wireOp",EDGE,"E25"),sQuery(id+"F0.wireOp",EDGE,"E27"),sQuery(id+"F0.wireOp",EDGE,"E29"),sQuery(id+"F0.wireOp",EDGE,"E30"),sQuery(id+"F0.wireOp",EDGE,"E31"),sQuery(id+"F0.wireOp",EDGE,"E35"),sQuery(id+"F0.wireOp",EDGE,"E36"),sQuery(id+"F0.wireOp",EDGE,"E37"),sQuery(id+"F0.wireOp",EDGE,"E38"),sQuery(id+"F0.wireOp",EDGE,"E39"),sQuery(id+"F0.wireOp",EDGE,"E40"),sQuery(id+"F0.wireOp",EDGE,"E41"),sQuery(id+"F0.wireOp",EDGE,"E42.bottom"),sQuery(id+"F0.wireOp",EDGE,"E42.left"),sQuery(id+"F0.wireOp",EDGE,"E42.right"),sQuery(id+"F0.wireOp",EDGE,"E45"),sQuery(id+"F0.wireOp",EDGE,"E46"),sQuery(id+"F0.wireOp",EDGE,"E47.MirrorCS"),sQuery(id+"F0.wireOp",EDGE,"E48.MirrorCS"),sQuery(id+"F0.wireOp",EDGE,"E51.trimOffspring"),sQuery(id+"F0.wireOp",EDGE,"E52.trimOffspring"),sQuery(id+"F0.wireOp",EDGE,"E54.bottom"),sQuery(id+"F0.wireOp",EDGE,"E54.top"),sQuery(id+"F0.wireOp",EDGE,"E54.left"),sQuery(id+"F0.wireOp",EDGE,"E57"),sQuery(id+"F0.wireOp",EDGE,"E58"),sQuery(id+"F0.wireOp",EDGE,"E60.MirrorCS"),sQuery(id+"F0.wireOp",EDGE,"E61.MirrorCS"),sQuery(id+"F0.wireOp",EDGE,"E62.trimOffspring")])],"isStart":true});
            var sketch = newSketch(context, id + "F21", { "sketchPlane" : qUnion([Q0])});
            skLineSegment(sketch, "E99", {"start": v(266.47, -11.31) * mm, "end": v(262, -11.31) * mm});
            skLineSegment(sketch, "E100", {"start": v(262, -11.31) * mm, "end": v(305.19, 59.73) * mm});
            skLineSegment(sketch, "E101", {"start": v(305.92, 53.6) * mm, "end": v(266.47, -11.31) * mm});
            skLineSegment(sketch, "E102", {"start": v(305.92, 53.6) * mm, "end": v(305.92, 61.01) * mm});
            skLineSegment(sketch, "E103", {"start": v(305.92, 61.01) * mm, "end": v(305.19, 59.73) * mm});
            skSolve(sketch);
        }
        {
            var Q0;
            Q0=makeQuery(id+"F21.imprint","IMPRINT",FACE,{"disambiguationData":[TD([[makeQuery(id+"F21.imprint","IMPRINT",EDGE,{"derivedFrom":sQuery(id+"F21.wireOp",EDGE,"E99")}),-1.0]])]});
            extrude(context, id + "F22", {"entities" : qUnion([Q0]), "operationType" : NewBodyOperationType.REMOVE, "oppositeDirection" : true, "depth" : 25 * mm, "offsetDistance" : 25 * mm});
        }
        {
            var Q0;
            Q0=makeQuery(id+"F22.boolean.opBoolean","MERGE",FACE,{"derivedFrom":[makeQuery(id+"F20.opExtrude","CAP_FACE",FACE,{"disambiguationData":[OSD([sQuery(id+"F19.wireOp",EDGE,"E94"),sQuery(id+"F19.wireOp",EDGE,"E95"),sQuery(id+"F19.wireOp",EDGE,"E96"),sQuery(id+"F19.wireOp",EDGE,"E97"),sQuery(id+"F19.wireOp",EDGE,"E98")])],"isStart":true})],"fromTools":[makeQuery(id+"F22.opExtrude","CAP_FACE",FACE,{"disambiguationData":[OSD([sQuery(id+"F21.wireOp",EDGE,"E99"),sQuery(id+"F21.wireOp",EDGE,"E100"),sQuery(id+"F21.wireOp",EDGE,"E101"),sQuery(id+"F21.wireOp",EDGE,"E102"),sQuery(id+"F21.wireOp",EDGE,"E103")])],"isStart":false})]});
            var sketch = newSketch(context, id + "F23", { "sketchPlane" : qUnion([Q0])});
            skCircle(sketch, "E104", {"center": v(293.15, 20.62) * mm, "radius": 8.22 * mm});
            skSolve(sketch);
        }
        {
            var Q0;
            Q0=qSketchRegion(id+"F23",true);
            extrude(context, id + "F24", {"entities" : qUnion([Q0]), "operationType" : NewBodyOperationType.REMOVE, "oppositeDirection" : true, "depth" : 2 * mm, "offsetDistance" : 25 * mm});
        }
        {
            var Q0;
            Q0=makeQuery(id+"F1.opExtrude","CAP_FACE",FACE,{"disambiguationData":[OSD([sQuery(id+"F0.wireOp",EDGE,"E0.top"),sQuery(id+"F0.wireOp",EDGE,"E0.left"),sQuery(id+"F0.wireOp",EDGE,"E1.bottom"),sQuery(id+"F0.wireOp",EDGE,"E1.top"),sQuery(id+"F0.wireOp",EDGE,"E1.left"),sQuery(id+"F0.wireOp",EDGE,"E1.right"),sQuery(id+"F0.wireOp",EDGE,"E2.top"),sQuery(id+"F0.wireOp",EDGE,"E3.trimOffspring"),sQuery(id+"F0.wireOp",EDGE,"E4"),sQuery(id+"F0.wireOp",EDGE,"E5"),sQuery(id+"F0.wireOp",EDGE,"E6.top"),sQuery(id+"F0.wireOp",EDGE,"E6.left"),sQuery(id+"F0.wireOp",EDGE,"E7.bottom"),sQuery(id+"F0.wireOp",EDGE,"E7.top"),sQuery(id+"F0.wireOp",EDGE,"E7.left"),sQuery(id+"F0.wireOp",EDGE,"E7.right"),sQuery(id+"F0.wireOp",EDGE,"E8.top"),sQuery(id+"F0.wireOp",EDGE,"E9.trimOffspring"),sQuery(id+"F0.wireOp",EDGE,"E10"),sQuery(id+"F0.wireOp",EDGE,"E11"),sQuery(id+"F0.wireOp",EDGE,"E12"),sQuery(id+"F0.wireOp",EDGE,"E14"),sQuery(id+"F0.wireOp",EDGE,"E15"),sQuery(id+"F0.wireOp",EDGE,"E16"),sQuery(id+"F0.wireOp",EDGE,"E18"),sQuery(id+"F0.wireOp",EDGE,"E25"),sQuery(id+"F0.wireOp",EDGE,"E27"),sQuery(id+"F0.wireOp",EDGE,"E29"),sQuery(id+"F0.wireOp",EDGE,"E30"),sQuery(id+"F0.wireOp",EDGE,"E31"),sQuery(id+"F0.wireOp",EDGE,"E35"),sQuery(id+"F0.wireOp",EDGE,"E36"),sQuery(id+"F0.wireOp",EDGE,"E37"),sQuery(id+"F0.wireOp",EDGE,"E38"),sQuery(id+"F0.wireOp",EDGE,"E39"),sQuery(id+"F0.wireOp",EDGE,"E40"),sQuery(id+"F0.wireOp",EDGE,"E41"),sQuery(id+"F0.wireOp",EDGE,"E42.bottom"),sQuery(id+"F0.wireOp",EDGE,"E42.left"),sQuery(id+"F0.wireOp",EDGE,"E42.right"),sQuery(id+"F0.wireOp",EDGE,"E45"),sQuery(id+"F0.wireOp",EDGE,"E46"),sQuery(id+"F0.wireOp",EDGE,"E47.MirrorCS"),sQuery(id+"F0.wireOp",EDGE,"E48.MirrorCS"),sQuery(id+"F0.wireOp",EDGE,"E51.trimOffspring"),sQuery(id+"F0.wireOp",EDGE,"E52.trimOffspring"),sQuery(id+"F0.wireOp",EDGE,"E54.bottom"),sQuery(id+"F0.wireOp",EDGE,"E54.top"),sQuery(id+"F0.wireOp",EDGE,"E54.left"),sQuery(id+"F0.wireOp",EDGE,"E57"),sQuery(id+"F0.wireOp",EDGE,"E58"),sQuery(id+"F0.wireOp",EDGE,"E60.MirrorCS"),sQuery(id+"F0.wireOp",EDGE,"E61.MirrorCS"),sQuery(id+"F0.wireOp",EDGE,"E62.trimOffspring")])],"isStart":true});
            var sketch = newSketch(context, id + "F25", { "sketchPlane" : qUnion([Q0])});
            skLineSegment(sketch, "E105", {"start": v(262, -11.31) * mm, "end": v(284.02, -11.31) * mm});
            skLineSegment(sketch, "E106", {"start": v(284.02, -11.31) * mm, "end": v(305.92, 24.73) * mm});
            skLineSegment(sketch, "E107", {"start": v(305.92, 24.73) * mm, "end": v(305.92, 61.01) * mm});
            skLineSegment(sketch, "E108", {"start": v(305.92, 61.01) * mm, "end": v(262, -11.31) * mm});
            skSolve(sketch);
        }
        {
            var Q0;
            Q0=qSketchRegion(id+"F25",true);
            extrude(context, id + "F26", {"entities" : qUnion([Q0]), "operationType" : NewBodyOperationType.ADD, "oppositeDirection" : true, "depth" : 2 * mm, "offsetDistance" : 25 * mm});
        }
        {
            var Q0;
            Q0=makeQuery(id+"F1.opExtrude","SWEPT_EDGE",EDGE,{"disambiguationData":[OSD([sQuery(id+"F0.wireOp",EDGE,"E0.top"),sQuery(id+"F0.wireOp",EDGE,"E0.left")])]});
            var Q1;
            Q1=makeQuery(id+"F1.opExtrude","SWEPT_EDGE",EDGE,{"disambiguationData":[OSD([sQuery(id+"F0.wireOp",EDGE,"E0.top"),sQuery(id+"F0.wireOp",EDGE,"E41")])]});
            var Q2;
            Q2=makeQuery(id+"F1.opExtrude","SWEPT_EDGE",EDGE,{"disambiguationData":[OSD([sQuery(id+"F0.wireOp",EDGE,"E4"),sQuery(id+"F0.wireOp",EDGE,"E37")])]});
            var Q3;
            Q3=makeQuery(id+"F1.opExtrude","SWEPT_EDGE",EDGE,{"disambiguationData":[OSD([sQuery(id+"F0.wireOp",EDGE,"E57"),sQuery(id+"F0.wireOp",EDGE,"E58")])]});
            var Q4;
            Q4=makeQuery(id+"F1.opExtrude","SWEPT_EDGE",EDGE,{"disambiguationData":[OSD([sQuery(id+"F0.wireOp",EDGE,"E60.MirrorCS"),sQuery(id+"F0.wireOp",EDGE,"E61.MirrorCS")])]});
            var Q5;
            Q5=makeQuery(id+"F1.opExtrude","SWEPT_EDGE",EDGE,{"disambiguationData":[OSD([sQuery(id+"F0.wireOp",EDGE,"E1.left"),sQuery(id+"F0.wireOp",EDGE,"E54.bottom")])]});
            var Q6;
            Q6=makeQuery(id+"F1.opExtrude","SWEPT_EDGE",EDGE,{"disambiguationData":[OSD([sQuery(id+"F0.wireOp",EDGE,"E3.trimOffspring"),sQuery(id+"F0.wireOp",EDGE,"E54.top")])]});
            var Q7;
            Q7=makeQuery(id+"F1.opExtrude","SWEPT_EDGE",EDGE,{"disambiguationData":[OSD([sQuery(id+"F0.wireOp",EDGE,"E45"),sQuery(id+"F0.wireOp",EDGE,"E46")])]});
            var Q8;
            Q8=makeQuery(id+"F1.opExtrude","SWEPT_EDGE",EDGE,{"disambiguationData":[OSD([sQuery(id+"F0.wireOp",EDGE,"E47.MirrorCS"),sQuery(id+"F0.wireOp",EDGE,"E48.MirrorCS")])]});
            var Q9;
            Q9=makeQuery(id+"F1.opExtrude","SWEPT_EDGE",EDGE,{"disambiguationData":[OSD([sQuery(id+"F0.wireOp",EDGE,"E7.bottom"),sQuery(id+"F0.wireOp",EDGE,"E42.left")])]});
            var Q10;
            Q10=makeQuery(id+"F1.opExtrude","SWEPT_EDGE",EDGE,{"disambiguationData":[OSD([sQuery(id+"F0.wireOp",EDGE,"E42.right"),sQuery(id+"F0.wireOp",EDGE,"E51.trimOffspring")])]});
            var Q11;
            Q11=makeQuery(id+"F1.opExtrude","SWEPT_EDGE",EDGE,{"disambiguationData":[OSD([sQuery(id+"F0.wireOp",EDGE,"E25"),sQuery(id+"F0.wireOp",EDGE,"E52.trimOffspring")])]});
            var Q12;
            Q12=makeQuery(id+"F1.opExtrude","SWEPT_EDGE",EDGE,{"disambiguationData":[OSD([sQuery(id+"F0.wireOp",EDGE,"E12"),sQuery(id+"F0.wireOp",EDGE,"E27")])]});
            var Q13;
            Q13=makeQuery(id+"F1.opExtrude","CAP_EDGE",EDGE,{"disambiguationData":[OSD([sQuery(id+"F0.wireOp",EDGE,"E39")])],"isStart":true});
            var Q14;
            Q14=makeQuery(id+"F1.opExtrude","CAP_EDGE",EDGE,{"disambiguationData":[OSD([sQuery(id+"F0.wireOp",EDGE,"E35")])],"isStart":true});
            var Q15;
            Q15=makeQuery(id+"F1.opExtrude","CAP_EDGE",EDGE,{"disambiguationData":[OSD([sQuery(id+"F0.wireOp",EDGE,"E39")])],"isStart":false});
            var Q16;
            Q16=makeQuery(id+"F1.opExtrude","CAP_EDGE",EDGE,{"disambiguationData":[OSD([sQuery(id+"F0.wireOp",EDGE,"E35")])],"isStart":false});
            var Q17;
            Q17=makeQuery(id+"F1.opExtrude","CAP_EDGE",EDGE,{"disambiguationData":[OSD([sQuery(id+"F0.wireOp",EDGE,"E30")])],"isStart":false});
            var Q18;
            Q18=makeQuery(id+"F1.opExtrude","CAP_EDGE",EDGE,{"disambiguationData":[OSD([sQuery(id+"F0.wireOp",EDGE,"E11")])],"isStart":false});
            var Q19;
            Q19=makeQuery(id+"F1.opExtrude","CAP_EDGE",EDGE,{"disambiguationData":[OSD([sQuery(id+"F0.wireOp",EDGE,"E30")])],"isStart":true});
            var Q20;
            Q20=makeQuery(id+"F1.opExtrude","CAP_EDGE",EDGE,{"disambiguationData":[OSD([sQuery(id+"F0.wireOp",EDGE,"E11")])],"isStart":true});
            var Q21;
            Q21=makeQuery(id+"F1.opExtrude","SWEPT_EDGE",EDGE,{"disambiguationData":[OSD([sQuery(id+"F0.wireOp",EDGE,"E6.top"),sQuery(id+"F0.wireOp",EDGE,"E6.left"),sQuery(id+"F0.wireOp",EDGE,"E15")])]});
            var Q22;
            Q22=makeQuery(id+"F1.opExtrude","SWEPT_EDGE",EDGE,{"disambiguationData":[OSD([sQuery(id+"F0.wireOp",EDGE,"E4"),sQuery(id+"F0.wireOp",EDGE,"E15"),sQuery(id+"F0.wireOp",EDGE,"E17")])]});
            var Q23;
            {var subQ0=sQuery(id+"F0.wireOp",EDGE,"E41");var subQ2=sQuery(id+"F0.wireOp",EDGE,"E38");var subQ4=sQuery(id+"F0.wireOp",EDGE,"E1.right");var subQ6=sQuery(id+"F0.wireOp",EDGE,"E61.MirrorCS");var subQ8=sQuery(id+"F0.wireOp",EDGE,"E0.top");var subQ9=makeQuery(id+"F1.opExtrude","SWEPT_FACE",FACE,{"disambiguationData":[OSD([subQ8])]});var subQ10=sQuery(id+"F12.wireOp",EDGE,"E89.bottom");var subQ11=sQuery(id+"F0.wireOp",EDGE,"E54.bottom");var subQ13=sQuery(id+"F0.wireOp",EDGE,"E39");var subQ15=sQuery(id+"F0.wireOp",EDGE,"E5");var subQ16=sQuery(id+"F0.wireOp",EDGE,"E0.left");var subQ18=sQuery(id+"F0.wireOp",EDGE,"E54.left");var subQ20=sQuery(id+"F0.wireOp",EDGE,"E40");var subQ22=sQuery(id+"F0.wireOp",EDGE,"E1.bottom");var subQ24=sQuery(id+"F0.wireOp",EDGE,"E1.left");var subQ26=sQuery(id+"F0.wireOp",EDGE,"E60.MirrorCS");var subQ28=sQuery(id+"F0.wireOp",EDGE,"E14");var subQ29=sQuery(id+"F0.wireOp",EDGE,"E1.top");Q23=makeQuery(id+"F18.opChamfer","BLEND_EDGE",EDGE,{"blendedFrom":[makeQuery(id+"F13.opExtrude","CAP_EDGE",EDGE,{"disambiguationData":[OSD([subQ10])],"isStart":false}),makeQuery(id+"F13.boolean.opBoolean","SPLIT",FACE,{"disambiguationData":[TD([subQ9])],"derivedFrom":makeQuery(id+"F3.boolean.opBoolean","SPLIT",FACE,{"disambiguationData":[TD([subQ9])],"derivedFrom":makeQuery(id+"F1.opExtrude","CAP_FACE",FACE,{"disambiguationData":[OSD([subQ8,subQ16,subQ22,subQ29,subQ24,subQ4,sQuery(id+"F0.wireOp",EDGE,"E2.top"),sQuery(id+"F0.wireOp",EDGE,"E3.trimOffspring"),sQuery(id+"F0.wireOp",EDGE,"E4"),subQ15,sQuery(id+"F0.wireOp",EDGE,"E6.top"),sQuery(id+"F0.wireOp",EDGE,"E6.left"),sQuery(id+"F0.wireOp",EDGE,"E7.bottom"),sQuery(id+"F0.wireOp",EDGE,"E7.top"),sQuery(id+"F0.wireOp",EDGE,"E7.left"),sQuery(id+"F0.wireOp",EDGE,"E7.right"),sQuery(id+"F0.wireOp",EDGE,"E8.top"),sQuery(id+"F0.wireOp",EDGE,"E9.trimOffspring"),sQuery(id+"F0.wireOp",EDGE,"E10"),sQuery(id+"F0.wireOp",EDGE,"E11"),sQuery(id+"F0.wireOp",EDGE,"E12"),subQ28,sQuery(id+"F0.wireOp",EDGE,"E15"),sQuery(id+"F0.wireOp",EDGE,"E16"),sQuery(id+"F0.wireOp",EDGE,"E18"),sQuery(id+"F0.wireOp",EDGE,"E25"),sQuery(id+"F0.wireOp",EDGE,"E27"),sQuery(id+"F0.wireOp",EDGE,"E29"),sQuery(id+"F0.wireOp",EDGE,"E30"),sQuery(id+"F0.wireOp",EDGE,"E31"),sQuery(id+"F0.wireOp",EDGE,"E35"),sQuery(id+"F0.wireOp",EDGE,"E36"),sQuery(id+"F0.wireOp",EDGE,"E37"),subQ2,subQ13,subQ20,subQ0,sQuery(id+"F0.wireOp",EDGE,"E42.bottom"),sQuery(id+"F0.wireOp",EDGE,"E42.left"),sQuery(id+"F0.wireOp",EDGE,"E42.right"),sQuery(id+"F0.wireOp",EDGE,"E45"),sQuery(id+"F0.wireOp",EDGE,"E46"),sQuery(id+"F0.wireOp",EDGE,"E47.MirrorCS"),sQuery(id+"F0.wireOp",EDGE,"E48.MirrorCS"),sQuery(id+"F0.wireOp",EDGE,"E51.trimOffspring"),sQuery(id+"F0.wireOp",EDGE,"E52.trimOffspring"),subQ11,sQuery(id+"F0.wireOp",EDGE,"E54.top"),subQ18,sQuery(id+"F0.wireOp",EDGE,"E57"),sQuery(id+"F0.wireOp",EDGE,"E58"),subQ26,subQ6,sQuery(id+"F0.wireOp",EDGE,"E62.trimOffspring")])],"isStart":false})})})],"blendedInto":[makeQuery(id+"F13.boolean.opBoolean","SPLIT",FACE,{"disambiguationData":[TD([subQ9])],"derivedFrom":makeQuery(id+"F3.boolean.opBoolean","SPLIT",FACE,{"disambiguationData":[TD([subQ9])],"derivedFrom":makeQuery(id+"F1.opExtrude","CAP_FACE",FACE,{"disambiguationData":[OSD([subQ8,subQ16,subQ22,subQ29,subQ24,subQ4,sQuery(id+"F0.wireOp",EDGE,"E2.top"),sQuery(id+"F0.wireOp",EDGE,"E3.trimOffspring"),sQuery(id+"F0.wireOp",EDGE,"E4"),subQ15,sQuery(id+"F0.wireOp",EDGE,"E6.top"),sQuery(id+"F0.wireOp",EDGE,"E6.left"),sQuery(id+"F0.wireOp",EDGE,"E7.bottom"),sQuery(id+"F0.wireOp",EDGE,"E7.top"),sQuery(id+"F0.wireOp",EDGE,"E7.left"),sQuery(id+"F0.wireOp",EDGE,"E7.right"),sQuery(id+"F0.wireOp",EDGE,"E8.top"),sQuery(id+"F0.wireOp",EDGE,"E9.trimOffspring"),sQuery(id+"F0.wireOp",EDGE,"E10"),sQuery(id+"F0.wireOp",EDGE,"E11"),sQuery(id+"F0.wireOp",EDGE,"E12"),subQ28,sQuery(id+"F0.wireOp",EDGE,"E15"),sQuery(id+"F0.wireOp",EDGE,"E16"),sQuery(id+"F0.wireOp",EDGE,"E18"),sQuery(id+"F0.wireOp",EDGE,"E25"),sQuery(id+"F0.wireOp",EDGE,"E27"),sQuery(id+"F0.wireOp",EDGE,"E29"),sQuery(id+"F0.wireOp",EDGE,"E30"),sQuery(id+"F0.wireOp",EDGE,"E31"),sQuery(id+"F0.wireOp",EDGE,"E35"),sQuery(id+"F0.wireOp",EDGE,"E36"),sQuery(id+"F0.wireOp",EDGE,"E37"),subQ2,subQ13,subQ20,subQ0,sQuery(id+"F0.wireOp",EDGE,"E42.bottom"),sQuery(id+"F0.wireOp",EDGE,"E42.left"),sQuery(id+"F0.wireOp",EDGE,"E42.right"),sQuery(id+"F0.wireOp",EDGE,"E45"),sQuery(id+"F0.wireOp",EDGE,"E46"),sQuery(id+"F0.wireOp",EDGE,"E47.MirrorCS"),sQuery(id+"F0.wireOp",EDGE,"E48.MirrorCS"),sQuery(id+"F0.wireOp",EDGE,"E51.trimOffspring"),sQuery(id+"F0.wireOp",EDGE,"E52.trimOffspring"),subQ11,sQuery(id+"F0.wireOp",EDGE,"E54.top"),subQ18,sQuery(id+"F0.wireOp",EDGE,"E57"),sQuery(id+"F0.wireOp",EDGE,"E58"),subQ26,subQ6,sQuery(id+"F0.wireOp",EDGE,"E62.trimOffspring")])],"isStart":false})})})]});}
            var Q24;
            {var subQ0=sQuery(id+"F0.wireOp",EDGE,"E27");var subQ5=sQuery(id+"F0.wireOp",EDGE,"E16");var subQ6=sQuery(id+"F0.wireOp",EDGE,"E14");var subQ7=sQuery(id+"F0.wireOp",EDGE,"E12");var subQ8=sQuery(id+"F0.wireOp",EDGE,"E11");var subQ9=sQuery(id+"F0.wireOp",EDGE,"E7.top");var subQ10=sQuery(id+"F0.wireOp",EDGE,"E10");var subQ11=sQuery(id+"F0.wireOp",EDGE,"E8.top");var subQ12=sQuery(id+"F0.wireOp",EDGE,"E9.trimOffspring");Q24=makeQuery(id+"F18.opChamfer","BLEND_EDGE",EDGE,{"blendedFrom":[makeQuery(id+"F11.opExtrude","CAP_EDGE",EDGE,{"disambiguationData":[OSD([sQuery(id+"F10.wireOp",EDGE,"E88.left")])],"isStart":false}),makeQuery(id+"F3.boolean.opBoolean","SPLIT",FACE,{"disambiguationData":[TD([makeQuery(id+"F1.opExtrude","SWEPT_FACE",FACE,{"disambiguationData":[OSD([subQ9])]})])],"derivedFrom":makeQuery(id+"F1.opExtrude","CAP_FACE",FACE,{"disambiguationData":[OSD([sQuery(id+"F0.wireOp",EDGE,"E0.top"),sQuery(id+"F0.wireOp",EDGE,"E0.left"),sQuery(id+"F0.wireOp",EDGE,"E1.bottom"),sQuery(id+"F0.wireOp",EDGE,"E1.top"),sQuery(id+"F0.wireOp",EDGE,"E1.left"),sQuery(id+"F0.wireOp",EDGE,"E1.right"),sQuery(id+"F0.wireOp",EDGE,"E2.top"),sQuery(id+"F0.wireOp",EDGE,"E3.trimOffspring"),sQuery(id+"F0.wireOp",EDGE,"E4"),sQuery(id+"F0.wireOp",EDGE,"E5"),sQuery(id+"F0.wireOp",EDGE,"E6.top"),sQuery(id+"F0.wireOp",EDGE,"E6.left"),sQuery(id+"F0.wireOp",EDGE,"E7.bottom"),subQ9,sQuery(id+"F0.wireOp",EDGE,"E7.left"),sQuery(id+"F0.wireOp",EDGE,"E7.right"),subQ11,subQ12,subQ10,subQ8,subQ7,subQ6,sQuery(id+"F0.wireOp",EDGE,"E15"),subQ5,sQuery(id+"F0.wireOp",EDGE,"E18"),sQuery(id+"F0.wireOp",EDGE,"E25"),subQ0,sQuery(id+"F0.wireOp",EDGE,"E29"),sQuery(id+"F0.wireOp",EDGE,"E30"),sQuery(id+"F0.wireOp",EDGE,"E31"),sQuery(id+"F0.wireOp",EDGE,"E35"),sQuery(id+"F0.wireOp",EDGE,"E36"),sQuery(id+"F0.wireOp",EDGE,"E37"),sQuery(id+"F0.wireOp",EDGE,"E38"),sQuery(id+"F0.wireOp",EDGE,"E39"),sQuery(id+"F0.wireOp",EDGE,"E40"),sQuery(id+"F0.wireOp",EDGE,"E41"),sQuery(id+"F0.wireOp",EDGE,"E42.bottom"),sQuery(id+"F0.wireOp",EDGE,"E42.left"),sQuery(id+"F0.wireOp",EDGE,"E42.right"),sQuery(id+"F0.wireOp",EDGE,"E45"),sQuery(id+"F0.wireOp",EDGE,"E46"),sQuery(id+"F0.wireOp",EDGE,"E47.MirrorCS"),sQuery(id+"F0.wireOp",EDGE,"E48.MirrorCS"),sQuery(id+"F0.wireOp",EDGE,"E51.trimOffspring"),sQuery(id+"F0.wireOp",EDGE,"E52.trimOffspring"),sQuery(id+"F0.wireOp",EDGE,"E54.bottom"),sQuery(id+"F0.wireOp",EDGE,"E54.top"),sQuery(id+"F0.wireOp",EDGE,"E54.left"),sQuery(id+"F0.wireOp",EDGE,"E57"),sQuery(id+"F0.wireOp",EDGE,"E58"),sQuery(id+"F0.wireOp",EDGE,"E60.MirrorCS"),sQuery(id+"F0.wireOp",EDGE,"E61.MirrorCS"),sQuery(id+"F0.wireOp",EDGE,"E62.trimOffspring")])],"isStart":false})})],"blendedInto":[makeQuery(id+"F3.boolean.opBoolean","SPLIT",FACE,{"disambiguationData":[TD([makeQuery(id+"F1.opExtrude","SWEPT_FACE",FACE,{"disambiguationData":[OSD([subQ9])]})])],"derivedFrom":makeQuery(id+"F1.opExtrude","CAP_FACE",FACE,{"disambiguationData":[OSD([sQuery(id+"F0.wireOp",EDGE,"E0.top"),sQuery(id+"F0.wireOp",EDGE,"E0.left"),sQuery(id+"F0.wireOp",EDGE,"E1.bottom"),sQuery(id+"F0.wireOp",EDGE,"E1.top"),sQuery(id+"F0.wireOp",EDGE,"E1.left"),sQuery(id+"F0.wireOp",EDGE,"E1.right"),sQuery(id+"F0.wireOp",EDGE,"E2.top"),sQuery(id+"F0.wireOp",EDGE,"E3.trimOffspring"),sQuery(id+"F0.wireOp",EDGE,"E4"),sQuery(id+"F0.wireOp",EDGE,"E5"),sQuery(id+"F0.wireOp",EDGE,"E6.top"),sQuery(id+"F0.wireOp",EDGE,"E6.left"),sQuery(id+"F0.wireOp",EDGE,"E7.bottom"),subQ9,sQuery(id+"F0.wireOp",EDGE,"E7.left"),sQuery(id+"F0.wireOp",EDGE,"E7.right"),subQ11,subQ12,subQ10,subQ8,subQ7,subQ6,sQuery(id+"F0.wireOp",EDGE,"E15"),subQ5,sQuery(id+"F0.wireOp",EDGE,"E18"),sQuery(id+"F0.wireOp",EDGE,"E25"),subQ0,sQuery(id+"F0.wireOp",EDGE,"E29"),sQuery(id+"F0.wireOp",EDGE,"E30"),sQuery(id+"F0.wireOp",EDGE,"E31"),sQuery(id+"F0.wireOp",EDGE,"E35"),sQuery(id+"F0.wireOp",EDGE,"E36"),sQuery(id+"F0.wireOp",EDGE,"E37"),sQuery(id+"F0.wireOp",EDGE,"E38"),sQuery(id+"F0.wireOp",EDGE,"E39"),sQuery(id+"F0.wireOp",EDGE,"E40"),sQuery(id+"F0.wireOp",EDGE,"E41"),sQuery(id+"F0.wireOp",EDGE,"E42.bottom"),sQuery(id+"F0.wireOp",EDGE,"E42.left"),sQuery(id+"F0.wireOp",EDGE,"E42.right"),sQuery(id+"F0.wireOp",EDGE,"E45"),sQuery(id+"F0.wireOp",EDGE,"E46"),sQuery(id+"F0.wireOp",EDGE,"E47.MirrorCS"),sQuery(id+"F0.wireOp",EDGE,"E48.MirrorCS"),sQuery(id+"F0.wireOp",EDGE,"E51.trimOffspring"),sQuery(id+"F0.wireOp",EDGE,"E52.trimOffspring"),sQuery(id+"F0.wireOp",EDGE,"E54.bottom"),sQuery(id+"F0.wireOp",EDGE,"E54.top"),sQuery(id+"F0.wireOp",EDGE,"E54.left"),sQuery(id+"F0.wireOp",EDGE,"E57"),sQuery(id+"F0.wireOp",EDGE,"E58"),sQuery(id+"F0.wireOp",EDGE,"E60.MirrorCS"),sQuery(id+"F0.wireOp",EDGE,"E61.MirrorCS"),sQuery(id+"F0.wireOp",EDGE,"E62.trimOffspring")])],"isStart":false})})]});}
            var Q25;
            {var subQ0=sQuery(id+"F10.wireOp",EDGE,"E88.left");Q25=makeQuery(id+"F18.opChamfer","BLEND_EDGE",EDGE,{"blendedFrom":[makeQuery(id+"F11.opExtrude","CAP_EDGE",EDGE,{"disambiguationData":[OSD([subQ0])],"isStart":false}),makeQuery(id+"F15.boolean.opBoolean","MERGE",FACE,{"derivedFrom":[makeQuery(id+"F13.boolean.opBoolean","MERGE",FACE,{"derivedFrom":[makeQuery(id+"F11.boolean.opBoolean","MERGE",FACE,{"derivedFrom":[makeQuery(id+"F3.opExtrude","CAP_FACE",FACE,{"disambiguationData":[OSD([sQuery(id+"F2.wireOp",EDGE,"E67"),sQuery(id+"F2.wireOp",EDGE,"E68"),sQuery(id+"F2.wireOp",EDGE,"E69"),sQuery(id+"F2.wireOp",EDGE,"E70"),sQuery(id+"F2.wireOp",EDGE,"E71")])],"isStart":false}),makeQuery(id+"F11.opExtrude","CAP_FACE",FACE,{"disambiguationData":[OSD([sQuery(id+"F10.wireOp",EDGE,"E88.bottom"),sQuery(id+"F10.wireOp",EDGE,"E88.top"),subQ0,sQuery(id+"F10.wireOp",EDGE,"E88.right")])],"isStart":false})]}),makeQuery(id+"F13.opExtrude","CAP_FACE",FACE,{"disambiguationData":[OSD([sQuery(id+"F12.wireOp",EDGE,"E89.bottom"),sQuery(id+"F12.wireOp",EDGE,"E89.top"),sQuery(id+"F12.wireOp",EDGE,"E89.left"),sQuery(id+"F12.wireOp",EDGE,"E89.right")])],"isStart":false})]}),makeQuery(id+"F15.opExtrude","CAP_FACE",FACE,{"disambiguationData":[OSD([sQuery(id+"F14.wireOp",EDGE,"E90.bottom"),sQuery(id+"F14.wireOp",EDGE,"E90.top"),sQuery(id+"F14.wireOp",EDGE,"E90.left"),sQuery(id+"F14.wireOp",EDGE,"E90.right")])],"isStart":false})]})],"blendedInto":[makeQuery(id+"F15.boolean.opBoolean","MERGE",FACE,{"derivedFrom":[makeQuery(id+"F13.boolean.opBoolean","MERGE",FACE,{"derivedFrom":[makeQuery(id+"F11.boolean.opBoolean","MERGE",FACE,{"derivedFrom":[makeQuery(id+"F3.opExtrude","CAP_FACE",FACE,{"disambiguationData":[OSD([sQuery(id+"F2.wireOp",EDGE,"E67"),sQuery(id+"F2.wireOp",EDGE,"E68"),sQuery(id+"F2.wireOp",EDGE,"E69"),sQuery(id+"F2.wireOp",EDGE,"E70"),sQuery(id+"F2.wireOp",EDGE,"E71")])],"isStart":false}),makeQuery(id+"F11.opExtrude","CAP_FACE",FACE,{"disambiguationData":[OSD([sQuery(id+"F10.wireOp",EDGE,"E88.bottom"),sQuery(id+"F10.wireOp",EDGE,"E88.top"),subQ0,sQuery(id+"F10.wireOp",EDGE,"E88.right")])],"isStart":false})]}),makeQuery(id+"F13.opExtrude","CAP_FACE",FACE,{"disambiguationData":[OSD([sQuery(id+"F12.wireOp",EDGE,"E89.bottom"),sQuery(id+"F12.wireOp",EDGE,"E89.top"),sQuery(id+"F12.wireOp",EDGE,"E89.left"),sQuery(id+"F12.wireOp",EDGE,"E89.right")])],"isStart":false})]}),makeQuery(id+"F15.opExtrude","CAP_FACE",FACE,{"disambiguationData":[OSD([sQuery(id+"F14.wireOp",EDGE,"E90.bottom"),sQuery(id+"F14.wireOp",EDGE,"E90.top"),sQuery(id+"F14.wireOp",EDGE,"E90.left"),sQuery(id+"F14.wireOp",EDGE,"E90.right")])],"isStart":false})]})]});}
            var Q26;
            {var subQ0=sQuery(id+"F12.wireOp",EDGE,"E89.bottom");Q26=makeQuery(id+"F18.opChamfer","BLEND_EDGE",EDGE,{"blendedFrom":[makeQuery(id+"F13.opExtrude","CAP_EDGE",EDGE,{"disambiguationData":[OSD([subQ0])],"isStart":false}),makeQuery(id+"F15.boolean.opBoolean","MERGE",FACE,{"derivedFrom":[makeQuery(id+"F13.boolean.opBoolean","MERGE",FACE,{"derivedFrom":[makeQuery(id+"F11.boolean.opBoolean","MERGE",FACE,{"derivedFrom":[makeQuery(id+"F3.opExtrude","CAP_FACE",FACE,{"disambiguationData":[OSD([sQuery(id+"F2.wireOp",EDGE,"E67"),sQuery(id+"F2.wireOp",EDGE,"E68"),sQuery(id+"F2.wireOp",EDGE,"E69"),sQuery(id+"F2.wireOp",EDGE,"E70"),sQuery(id+"F2.wireOp",EDGE,"E71")])],"isStart":false}),makeQuery(id+"F11.opExtrude","CAP_FACE",FACE,{"disambiguationData":[OSD([sQuery(id+"F10.wireOp",EDGE,"E88.bottom"),sQuery(id+"F10.wireOp",EDGE,"E88.top"),sQuery(id+"F10.wireOp",EDGE,"E88.left"),sQuery(id+"F10.wireOp",EDGE,"E88.right")])],"isStart":false})]}),makeQuery(id+"F13.opExtrude","CAP_FACE",FACE,{"disambiguationData":[OSD([subQ0,sQuery(id+"F12.wireOp",EDGE,"E89.top"),sQuery(id+"F12.wireOp",EDGE,"E89.left"),sQuery(id+"F12.wireOp",EDGE,"E89.right")])],"isStart":false})]}),makeQuery(id+"F15.opExtrude","CAP_FACE",FACE,{"disambiguationData":[OSD([sQuery(id+"F14.wireOp",EDGE,"E90.bottom"),sQuery(id+"F14.wireOp",EDGE,"E90.top"),sQuery(id+"F14.wireOp",EDGE,"E90.left"),sQuery(id+"F14.wireOp",EDGE,"E90.right")])],"isStart":false})]})],"blendedInto":[makeQuery(id+"F15.boolean.opBoolean","MERGE",FACE,{"derivedFrom":[makeQuery(id+"F13.boolean.opBoolean","MERGE",FACE,{"derivedFrom":[makeQuery(id+"F11.boolean.opBoolean","MERGE",FACE,{"derivedFrom":[makeQuery(id+"F3.opExtrude","CAP_FACE",FACE,{"disambiguationData":[OSD([sQuery(id+"F2.wireOp",EDGE,"E67"),sQuery(id+"F2.wireOp",EDGE,"E68"),sQuery(id+"F2.wireOp",EDGE,"E69"),sQuery(id+"F2.wireOp",EDGE,"E70"),sQuery(id+"F2.wireOp",EDGE,"E71")])],"isStart":false}),makeQuery(id+"F11.opExtrude","CAP_FACE",FACE,{"disambiguationData":[OSD([sQuery(id+"F10.wireOp",EDGE,"E88.bottom"),sQuery(id+"F10.wireOp",EDGE,"E88.top"),sQuery(id+"F10.wireOp",EDGE,"E88.left"),sQuery(id+"F10.wireOp",EDGE,"E88.right")])],"isStart":false})]}),makeQuery(id+"F13.opExtrude","CAP_FACE",FACE,{"disambiguationData":[OSD([subQ0,sQuery(id+"F12.wireOp",EDGE,"E89.top"),sQuery(id+"F12.wireOp",EDGE,"E89.left"),sQuery(id+"F12.wireOp",EDGE,"E89.right")])],"isStart":false})]}),makeQuery(id+"F15.opExtrude","CAP_FACE",FACE,{"disambiguationData":[OSD([sQuery(id+"F14.wireOp",EDGE,"E90.bottom"),sQuery(id+"F14.wireOp",EDGE,"E90.top"),sQuery(id+"F14.wireOp",EDGE,"E90.left"),sQuery(id+"F14.wireOp",EDGE,"E90.right")])],"isStart":false})]})]});}
            fillet(context, id + "F27", {"entities" : qUnion([Q0, Q1, Q2, Q3, Q4, Q5, Q6, Q7, Q8, Q9, Q10, Q11, Q12, Q13, Q14, Q15, Q16, Q17, Q18, Q19, Q20, Q21, Q22, Q23, Q24, Q25, Q26]), "tangentPropagation" : true, "radius" : 5 * mm, "defaultsChanged" : false, "vertexSettings" : [], "allowEdgeOverflow" : false});
        }
        {
            var Q0;
            Q0=makeQuery(id+"F26.boolean.opBoolean","MERGE",FACE,{"derivedFrom":[makeQuery(id+"F1.opExtrude","CAP_FACE",FACE,{"disambiguationData":[OSD([sQuery(id+"F0.wireOp",EDGE,"E0.top"),sQuery(id+"F0.wireOp",EDGE,"E0.left"),sQuery(id+"F0.wireOp",EDGE,"E1.bottom"),sQuery(id+"F0.wireOp",EDGE,"E1.top"),sQuery(id+"F0.wireOp",EDGE,"E1.left"),sQuery(id+"F0.wireOp",EDGE,"E1.right"),sQuery(id+"F0.wireOp",EDGE,"E2.top"),sQuery(id+"F0.wireOp",EDGE,"E3.trimOffspring"),sQuery(id+"F0.wireOp",EDGE,"E4"),sQuery(id+"F0.wireOp",EDGE,"E5"),sQuery(id+"F0.wireOp",EDGE,"E6.top"),sQuery(id+"F0.wireOp",EDGE,"E6.left"),sQuery(id+"F0.wireOp",EDGE,"E7.bottom"),sQuery(id+"F0.wireOp",EDGE,"E7.top"),sQuery(id+"F0.wireOp",EDGE,"E7.left"),sQuery(id+"F0.wireOp",EDGE,"E7.right"),sQuery(id+"F0.wireOp",EDGE,"E8.top"),sQuery(id+"F0.wireOp",EDGE,"E9.trimOffspring"),sQuery(id+"F0.wireOp",EDGE,"E10"),sQuery(id+"F0.wireOp",EDGE,"E11"),sQuery(id+"F0.wireOp",EDGE,"E12"),sQuery(id+"F0.wireOp",EDGE,"E14"),sQuery(id+"F0.wireOp",EDGE,"E15"),sQuery(id+"F0.wireOp",EDGE,"E16"),sQuery(id+"F0.wireOp",EDGE,"E18"),sQuery(id+"F0.wireOp",EDGE,"E25"),sQuery(id+"F0.wireOp",EDGE,"E27"),sQuery(id+"F0.wireOp",EDGE,"E29"),sQuery(id+"F0.wireOp",EDGE,"E30"),sQuery(id+"F0.wireOp",EDGE,"E31"),sQuery(id+"F0.wireOp",EDGE,"E35"),sQuery(id+"F0.wireOp",EDGE,"E36"),sQuery(id+"F0.wireOp",EDGE,"E37"),sQuery(id+"F0.wireOp",EDGE,"E38"),sQuery(id+"F0.wireOp",EDGE,"E39"),sQuery(id+"F0.wireOp",EDGE,"E40"),sQuery(id+"F0.wireOp",EDGE,"E41"),sQuery(id+"F0.wireOp",EDGE,"E42.bottom"),sQuery(id+"F0.wireOp",EDGE,"E42.left"),sQuery(id+"F0.wireOp",EDGE,"E42.right"),sQuery(id+"F0.wireOp",EDGE,"E45"),sQuery(id+"F0.wireOp",EDGE,"E46"),sQuery(id+"F0.wireOp",EDGE,"E47.MirrorCS"),sQuery(id+"F0.wireOp",EDGE,"E48.MirrorCS"),sQuery(id+"F0.wireOp",EDGE,"E51.trimOffspring"),sQuery(id+"F0.wireOp",EDGE,"E52.trimOffspring"),sQuery(id+"F0.wireOp",EDGE,"E54.bottom"),sQuery(id+"F0.wireOp",EDGE,"E54.top"),sQuery(id+"F0.wireOp",EDGE,"E54.left"),sQuery(id+"F0.wireOp",EDGE,"E57"),sQuery(id+"F0.wireOp",EDGE,"E58"),sQuery(id+"F0.wireOp",EDGE,"E60.MirrorCS"),sQuery(id+"F0.wireOp",EDGE,"E61.MirrorCS"),sQuery(id+"F0.wireOp",EDGE,"E62.trimOffspring")])],"isStart":true}),makeQuery(id+"F26.opExtrude","CAP_FACE",FACE,{"disambiguationData":[OSD([sQuery(id+"F25.wireOp",EDGE,"E105"),sQuery(id+"F25.wireOp",EDGE,"E106"),sQuery(id+"F25.wireOp",EDGE,"E107"),sQuery(id+"F25.wireOp",EDGE,"E108")])],"isStart":true})]});
            var Q1;
            Q1=makeQuery(id+"F1.opExtrude","CAP_EDGE",EDGE,{"disambiguationData":[OSD([sQuery(id+"F0.wireOp",EDGE,"E0.top")])],"isStart":false});
            var Q2;
            Q2=makeQuery(id+"F1.opExtrude","CAP_EDGE",EDGE,{"disambiguationData":[OSD([sQuery(id+"F0.wireOp",EDGE,"E46"),sQuery(id+"F0.wireOp",EDGE,"E47.MirrorCS")])],"isStart":false});
            var Q3;
            Q3=makeQuery(id+"F1.opExtrude","CAP_EDGE",EDGE,{"disambiguationData":[OSD([sQuery(id+"F0.wireOp",EDGE,"E12")])],"isStart":false});
            var Q4;
            Q4=makeQuery(id+"F1.opExtrude","CAP_EDGE",EDGE,{"disambiguationData":[OSD([sQuery(id+"F0.wireOp",EDGE,"E42.bottom")])],"isStart":false});
            var Q5;
            {var subQ0=sQuery(id+"F0.wireOp",EDGE,"E57");var subQ2=sQuery(id+"F0.wireOp",EDGE,"E54.top");var subQ4=sQuery(id+"F0.wireOp",EDGE,"E37");var subQ6=sQuery(id+"F0.wireOp",EDGE,"E4");var subQ8=sQuery(id+"F0.wireOp",EDGE,"E15");var subQ10=sQuery(id+"F0.wireOp",EDGE,"E35");var subQ12=sQuery(id+"F0.wireOp",EDGE,"E3.trimOffspring");var subQ15=sQuery(id+"F0.wireOp",EDGE,"E1.top");var subQ16=makeQuery(id+"F1.opExtrude","SWEPT_FACE",FACE,{"disambiguationData":[OSD([subQ15])]});var subQ17=sQuery(id+"F0.wireOp",EDGE,"E58");var subQ19=sQuery(id+"F0.wireOp",EDGE,"E2.top");var subQ20=makeQuery(id+"F1.opExtrude","SWEPT_FACE",FACE,{"disambiguationData":[OSD([subQ19])]});var subQ21=sQuery(id+"F0.wireOp",EDGE,"E62.trimOffspring");var subQ23=sQuery(id+"F0.wireOp",EDGE,"E36");var subQ25=sQuery(id+"F0.wireOp",EDGE,"E30");var subQ26=sQuery(id+"F0.wireOp",EDGE,"E29");var subQ29=sQuery(id+"F0.wireOp",EDGE,"E25");var subQ30=sQuery(id+"F0.wireOp",EDGE,"E18");var subQ31=sQuery(id+"F0.wireOp",EDGE,"E16");var subQ32=sQuery(id+"F0.wireOp",EDGE,"E31");var subQ33=sQuery(id+"F0.wireOp",EDGE,"E42.bottom");var subQ34=sQuery(id+"F0.wireOp",EDGE,"E7.left");var subQ35=sQuery(id+"F0.wireOp",EDGE,"E6.top");var subQ36=sQuery(id+"F0.wireOp",EDGE,"E6.left");var subQ37=sQuery(id+"F0.wireOp",EDGE,"E7.bottom");var subQ38=sQuery(id+"F0.wireOp",EDGE,"E42.left");var subQ39=sQuery(id+"F0.wireOp",EDGE,"E7.right");var subQ40=sQuery(id+"F0.wireOp",EDGE,"E42.right");var subQ41=sQuery(id+"F0.wireOp",EDGE,"E45");var subQ42=sQuery(id+"F0.wireOp",EDGE,"E47.MirrorCS");var subQ43=sQuery(id+"F0.wireOp",EDGE,"E46");var subQ44=sQuery(id+"F0.wireOp",EDGE,"E48.MirrorCS");var subQ45=sQuery(id+"F0.wireOp",EDGE,"E51.trimOffspring");var subQ46=sQuery(id+"F0.wireOp",EDGE,"E52.trimOffspring");Q5=makeQuery(id+"F27.opFillet","BLEND_EDGE",EDGE,{"blendedFrom":[makeQuery(id+"F1.opExtrude","SWEPT_EDGE",EDGE,{"disambiguationData":[OSD([subQ6,subQ4])]}),makeQuery(id+"F20.boolean.opBoolean","SPLIT",FACE,{"disambiguationData":[TD([subQ16])],"derivedFrom":makeQuery(id+"F3.boolean.opBoolean","SPLIT",FACE,{"disambiguationData":[TD([subQ20])],"derivedFrom":makeQuery(id+"F1.opExtrude","CAP_FACE",FACE,{"disambiguationData":[OSD([sQuery(id+"F0.wireOp",EDGE,"E0.top"),sQuery(id+"F0.wireOp",EDGE,"E0.left"),sQuery(id+"F0.wireOp",EDGE,"E1.bottom"),subQ15,sQuery(id+"F0.wireOp",EDGE,"E1.left"),sQuery(id+"F0.wireOp",EDGE,"E1.right"),subQ19,subQ12,subQ6,sQuery(id+"F0.wireOp",EDGE,"E5"),subQ35,subQ36,subQ37,sQuery(id+"F0.wireOp",EDGE,"E7.top"),subQ34,subQ39,sQuery(id+"F0.wireOp",EDGE,"E8.top"),sQuery(id+"F0.wireOp",EDGE,"E9.trimOffspring"),sQuery(id+"F0.wireOp",EDGE,"E10"),sQuery(id+"F0.wireOp",EDGE,"E11"),sQuery(id+"F0.wireOp",EDGE,"E12"),sQuery(id+"F0.wireOp",EDGE,"E14"),subQ8,subQ31,subQ30,subQ29,sQuery(id+"F0.wireOp",EDGE,"E27"),subQ26,subQ25,subQ32,subQ10,subQ23,subQ4,sQuery(id+"F0.wireOp",EDGE,"E38"),sQuery(id+"F0.wireOp",EDGE,"E39"),sQuery(id+"F0.wireOp",EDGE,"E40"),sQuery(id+"F0.wireOp",EDGE,"E41"),subQ33,subQ38,subQ40,subQ41,subQ43,subQ42,subQ44,subQ45,subQ46,sQuery(id+"F0.wireOp",EDGE,"E54.bottom"),subQ2,sQuery(id+"F0.wireOp",EDGE,"E54.left"),subQ0,subQ17,sQuery(id+"F0.wireOp",EDGE,"E60.MirrorCS"),sQuery(id+"F0.wireOp",EDGE,"E61.MirrorCS"),subQ21])],"isStart":false})})})],"blendedInto":[makeQuery(id+"F20.boolean.opBoolean","SPLIT",FACE,{"disambiguationData":[TD([subQ16])],"derivedFrom":makeQuery(id+"F3.boolean.opBoolean","SPLIT",FACE,{"disambiguationData":[TD([subQ20])],"derivedFrom":makeQuery(id+"F1.opExtrude","CAP_FACE",FACE,{"disambiguationData":[OSD([sQuery(id+"F0.wireOp",EDGE,"E0.top"),sQuery(id+"F0.wireOp",EDGE,"E0.left"),sQuery(id+"F0.wireOp",EDGE,"E1.bottom"),subQ15,sQuery(id+"F0.wireOp",EDGE,"E1.left"),sQuery(id+"F0.wireOp",EDGE,"E1.right"),subQ19,subQ12,subQ6,sQuery(id+"F0.wireOp",EDGE,"E5"),subQ35,subQ36,subQ37,sQuery(id+"F0.wireOp",EDGE,"E7.top"),subQ34,subQ39,sQuery(id+"F0.wireOp",EDGE,"E8.top"),sQuery(id+"F0.wireOp",EDGE,"E9.trimOffspring"),sQuery(id+"F0.wireOp",EDGE,"E10"),sQuery(id+"F0.wireOp",EDGE,"E11"),sQuery(id+"F0.wireOp",EDGE,"E12"),sQuery(id+"F0.wireOp",EDGE,"E14"),subQ8,subQ31,subQ30,subQ29,sQuery(id+"F0.wireOp",EDGE,"E27"),subQ26,subQ25,subQ32,subQ10,subQ23,subQ4,sQuery(id+"F0.wireOp",EDGE,"E38"),sQuery(id+"F0.wireOp",EDGE,"E39"),sQuery(id+"F0.wireOp",EDGE,"E40"),sQuery(id+"F0.wireOp",EDGE,"E41"),subQ33,subQ38,subQ40,subQ41,subQ43,subQ42,subQ44,subQ45,subQ46,sQuery(id+"F0.wireOp",EDGE,"E54.bottom"),subQ2,sQuery(id+"F0.wireOp",EDGE,"E54.left"),subQ0,subQ17,sQuery(id+"F0.wireOp",EDGE,"E60.MirrorCS"),sQuery(id+"F0.wireOp",EDGE,"E61.MirrorCS"),subQ21])],"isStart":false})})})]});}
            var Q6;
            {var subQ0=sQuery(id+"F0.wireOp",EDGE,"E31");var subQ2=sQuery(id+"F0.wireOp",EDGE,"E30");var subQ4=sQuery(id+"F0.wireOp",EDGE,"E29");var subQ6=sQuery(id+"F0.wireOp",EDGE,"E15");var subQ8=sQuery(id+"F0.wireOp",EDGE,"E6.top");var subQ9=makeQuery(id+"F1.opExtrude","SWEPT_FACE",FACE,{"disambiguationData":[OSD([subQ8])]});var subQ10=sQuery(id+"F0.wireOp",EDGE,"E42.bottom");var subQ12=sQuery(id+"F0.wireOp",EDGE,"E7.left");var subQ14=sQuery(id+"F0.wireOp",EDGE,"E7.right");var subQ16=sQuery(id+"F0.wireOp",EDGE,"E42.left");var subQ18=sQuery(id+"F0.wireOp",EDGE,"E7.bottom");var subQ20=sQuery(id+"F0.wireOp",EDGE,"E25");var subQ22=sQuery(id+"F0.wireOp",EDGE,"E42.right");var subQ24=sQuery(id+"F0.wireOp",EDGE,"E45");var subQ26=sQuery(id+"F0.wireOp",EDGE,"E47.MirrorCS");var subQ27=sQuery(id+"F0.wireOp",EDGE,"E46");var subQ29=sQuery(id+"F0.wireOp",EDGE,"E48.MirrorCS");var subQ31=sQuery(id+"F0.wireOp",EDGE,"E51.trimOffspring");var subQ33=sQuery(id+"F0.wireOp",EDGE,"E52.trimOffspring");var subQ37=sQuery(id+"F0.wireOp",EDGE,"E18");var subQ38=sQuery(id+"F0.wireOp",EDGE,"E16");var subQ39=sQuery(id+"F0.wireOp",EDGE,"E35");var subQ40=sQuery(id+"F0.wireOp",EDGE,"E3.trimOffspring");var subQ41=sQuery(id+"F0.wireOp",EDGE,"E2.top");var subQ42=sQuery(id+"F0.wireOp",EDGE,"E36");var subQ43=sQuery(id+"F0.wireOp",EDGE,"E4");var subQ45=sQuery(id+"F0.wireOp",EDGE,"E1.top");var subQ46=sQuery(id+"F0.wireOp",EDGE,"E37");var subQ47=sQuery(id+"F0.wireOp",EDGE,"E6.left");var subQ48=sQuery(id+"F0.wireOp",EDGE,"E54.top");var subQ49=sQuery(id+"F0.wireOp",EDGE,"E57");var subQ50=sQuery(id+"F0.wireOp",EDGE,"E58");var subQ51=sQuery(id+"F0.wireOp",EDGE,"E62.trimOffspring");Q6=makeQuery(id+"F27.opFillet","BLEND_EDGE",EDGE,{"blendedFrom":[makeQuery(id+"F1.opExtrude","SWEPT_EDGE",EDGE,{"disambiguationData":[OSD([subQ22,subQ31])]}),makeQuery(id+"F20.boolean.opBoolean","SPLIT",FACE,{"disambiguationData":[TD([subQ9])],"derivedFrom":makeQuery(id+"F3.boolean.opBoolean","SPLIT",FACE,{"disambiguationData":[TD([makeQuery(id+"F1.opExtrude","SWEPT_FACE",FACE,{"disambiguationData":[OSD([subQ41])]})])],"derivedFrom":makeQuery(id+"F1.opExtrude","CAP_FACE",FACE,{"disambiguationData":[OSD([sQuery(id+"F0.wireOp",EDGE,"E0.top"),sQuery(id+"F0.wireOp",EDGE,"E0.left"),sQuery(id+"F0.wireOp",EDGE,"E1.bottom"),subQ45,sQuery(id+"F0.wireOp",EDGE,"E1.left"),sQuery(id+"F0.wireOp",EDGE,"E1.right"),subQ41,subQ40,subQ43,sQuery(id+"F0.wireOp",EDGE,"E5"),subQ8,subQ47,subQ18,sQuery(id+"F0.wireOp",EDGE,"E7.top"),subQ12,subQ14,sQuery(id+"F0.wireOp",EDGE,"E8.top"),sQuery(id+"F0.wireOp",EDGE,"E9.trimOffspring"),sQuery(id+"F0.wireOp",EDGE,"E10"),sQuery(id+"F0.wireOp",EDGE,"E11"),sQuery(id+"F0.wireOp",EDGE,"E12"),sQuery(id+"F0.wireOp",EDGE,"E14"),subQ6,subQ38,subQ37,subQ20,sQuery(id+"F0.wireOp",EDGE,"E27"),subQ4,subQ2,subQ0,subQ39,subQ42,subQ46,sQuery(id+"F0.wireOp",EDGE,"E38"),sQuery(id+"F0.wireOp",EDGE,"E39"),sQuery(id+"F0.wireOp",EDGE,"E40"),sQuery(id+"F0.wireOp",EDGE,"E41"),subQ10,subQ16,subQ22,subQ24,subQ27,subQ26,subQ29,subQ31,subQ33,sQuery(id+"F0.wireOp",EDGE,"E54.bottom"),subQ48,sQuery(id+"F0.wireOp",EDGE,"E54.left"),subQ49,subQ50,sQuery(id+"F0.wireOp",EDGE,"E60.MirrorCS"),sQuery(id+"F0.wireOp",EDGE,"E61.MirrorCS"),subQ51])],"isStart":false})})})],"blendedInto":[makeQuery(id+"F20.boolean.opBoolean","SPLIT",FACE,{"disambiguationData":[TD([subQ9])],"derivedFrom":makeQuery(id+"F3.boolean.opBoolean","SPLIT",FACE,{"disambiguationData":[TD([makeQuery(id+"F1.opExtrude","SWEPT_FACE",FACE,{"disambiguationData":[OSD([subQ41])]})])],"derivedFrom":makeQuery(id+"F1.opExtrude","CAP_FACE",FACE,{"disambiguationData":[OSD([sQuery(id+"F0.wireOp",EDGE,"E0.top"),sQuery(id+"F0.wireOp",EDGE,"E0.left"),sQuery(id+"F0.wireOp",EDGE,"E1.bottom"),subQ45,sQuery(id+"F0.wireOp",EDGE,"E1.left"),sQuery(id+"F0.wireOp",EDGE,"E1.right"),subQ41,subQ40,subQ43,sQuery(id+"F0.wireOp",EDGE,"E5"),subQ8,subQ47,subQ18,sQuery(id+"F0.wireOp",EDGE,"E7.top"),subQ12,subQ14,sQuery(id+"F0.wireOp",EDGE,"E8.top"),sQuery(id+"F0.wireOp",EDGE,"E9.trimOffspring"),sQuery(id+"F0.wireOp",EDGE,"E10"),sQuery(id+"F0.wireOp",EDGE,"E11"),sQuery(id+"F0.wireOp",EDGE,"E12"),sQuery(id+"F0.wireOp",EDGE,"E14"),subQ6,subQ38,subQ37,subQ20,sQuery(id+"F0.wireOp",EDGE,"E27"),subQ4,subQ2,subQ0,subQ39,subQ42,subQ46,sQuery(id+"F0.wireOp",EDGE,"E38"),sQuery(id+"F0.wireOp",EDGE,"E39"),sQuery(id+"F0.wireOp",EDGE,"E40"),sQuery(id+"F0.wireOp",EDGE,"E41"),subQ10,subQ16,subQ22,subQ24,subQ27,subQ26,subQ29,subQ31,subQ33,sQuery(id+"F0.wireOp",EDGE,"E54.bottom"),subQ48,sQuery(id+"F0.wireOp",EDGE,"E54.left"),subQ49,subQ50,sQuery(id+"F0.wireOp",EDGE,"E60.MirrorCS"),sQuery(id+"F0.wireOp",EDGE,"E61.MirrorCS"),subQ51])],"isStart":false})})})]});}
            var Q7;
            {var subQ0=sQuery(id+"F0.wireOp",EDGE,"E31");var subQ2=sQuery(id+"F0.wireOp",EDGE,"E30");var subQ4=sQuery(id+"F0.wireOp",EDGE,"E29");var subQ6=sQuery(id+"F0.wireOp",EDGE,"E15");var subQ8=sQuery(id+"F0.wireOp",EDGE,"E6.top");var subQ9=makeQuery(id+"F1.opExtrude","SWEPT_FACE",FACE,{"disambiguationData":[OSD([subQ8])]});var subQ10=sQuery(id+"F0.wireOp",EDGE,"E42.bottom");var subQ12=sQuery(id+"F0.wireOp",EDGE,"E7.left");var subQ14=sQuery(id+"F0.wireOp",EDGE,"E7.right");var subQ16=sQuery(id+"F0.wireOp",EDGE,"E42.left");var subQ18=sQuery(id+"F0.wireOp",EDGE,"E7.bottom");var subQ20=sQuery(id+"F0.wireOp",EDGE,"E25");var subQ22=sQuery(id+"F0.wireOp",EDGE,"E42.right");var subQ24=sQuery(id+"F0.wireOp",EDGE,"E45");var subQ26=sQuery(id+"F0.wireOp",EDGE,"E47.MirrorCS");var subQ27=sQuery(id+"F0.wireOp",EDGE,"E46");var subQ29=sQuery(id+"F0.wireOp",EDGE,"E48.MirrorCS");var subQ31=sQuery(id+"F0.wireOp",EDGE,"E51.trimOffspring");var subQ33=sQuery(id+"F0.wireOp",EDGE,"E52.trimOffspring");var subQ37=sQuery(id+"F0.wireOp",EDGE,"E18");var subQ38=sQuery(id+"F0.wireOp",EDGE,"E16");var subQ39=sQuery(id+"F0.wireOp",EDGE,"E35");var subQ40=sQuery(id+"F0.wireOp",EDGE,"E3.trimOffspring");var subQ41=sQuery(id+"F0.wireOp",EDGE,"E2.top");var subQ42=sQuery(id+"F0.wireOp",EDGE,"E36");var subQ43=sQuery(id+"F0.wireOp",EDGE,"E4");var subQ45=sQuery(id+"F0.wireOp",EDGE,"E1.top");var subQ46=sQuery(id+"F0.wireOp",EDGE,"E37");var subQ47=sQuery(id+"F0.wireOp",EDGE,"E6.left");var subQ48=sQuery(id+"F0.wireOp",EDGE,"E54.top");var subQ49=sQuery(id+"F0.wireOp",EDGE,"E57");var subQ50=sQuery(id+"F0.wireOp",EDGE,"E58");var subQ51=sQuery(id+"F0.wireOp",EDGE,"E62.trimOffspring");Q7=makeQuery(id+"F27.opFillet","BLEND_EDGE",EDGE,{"blendedFrom":[makeQuery(id+"F1.opExtrude","SWEPT_EDGE",EDGE,{"disambiguationData":[OSD([subQ18,subQ16])]}),makeQuery(id+"F20.boolean.opBoolean","SPLIT",FACE,{"disambiguationData":[TD([subQ9])],"derivedFrom":makeQuery(id+"F3.boolean.opBoolean","SPLIT",FACE,{"disambiguationData":[TD([makeQuery(id+"F1.opExtrude","SWEPT_FACE",FACE,{"disambiguationData":[OSD([subQ41])]})])],"derivedFrom":makeQuery(id+"F1.opExtrude","CAP_FACE",FACE,{"disambiguationData":[OSD([sQuery(id+"F0.wireOp",EDGE,"E0.top"),sQuery(id+"F0.wireOp",EDGE,"E0.left"),sQuery(id+"F0.wireOp",EDGE,"E1.bottom"),subQ45,sQuery(id+"F0.wireOp",EDGE,"E1.left"),sQuery(id+"F0.wireOp",EDGE,"E1.right"),subQ41,subQ40,subQ43,sQuery(id+"F0.wireOp",EDGE,"E5"),subQ8,subQ47,subQ18,sQuery(id+"F0.wireOp",EDGE,"E7.top"),subQ12,subQ14,sQuery(id+"F0.wireOp",EDGE,"E8.top"),sQuery(id+"F0.wireOp",EDGE,"E9.trimOffspring"),sQuery(id+"F0.wireOp",EDGE,"E10"),sQuery(id+"F0.wireOp",EDGE,"E11"),sQuery(id+"F0.wireOp",EDGE,"E12"),sQuery(id+"F0.wireOp",EDGE,"E14"),subQ6,subQ38,subQ37,subQ20,sQuery(id+"F0.wireOp",EDGE,"E27"),subQ4,subQ2,subQ0,subQ39,subQ42,subQ46,sQuery(id+"F0.wireOp",EDGE,"E38"),sQuery(id+"F0.wireOp",EDGE,"E39"),sQuery(id+"F0.wireOp",EDGE,"E40"),sQuery(id+"F0.wireOp",EDGE,"E41"),subQ10,subQ16,subQ22,subQ24,subQ27,subQ26,subQ29,subQ31,subQ33,sQuery(id+"F0.wireOp",EDGE,"E54.bottom"),subQ48,sQuery(id+"F0.wireOp",EDGE,"E54.left"),subQ49,subQ50,sQuery(id+"F0.wireOp",EDGE,"E60.MirrorCS"),sQuery(id+"F0.wireOp",EDGE,"E61.MirrorCS"),subQ51])],"isStart":false})})})],"blendedInto":[makeQuery(id+"F20.boolean.opBoolean","SPLIT",FACE,{"disambiguationData":[TD([subQ9])],"derivedFrom":makeQuery(id+"F3.boolean.opBoolean","SPLIT",FACE,{"disambiguationData":[TD([makeQuery(id+"F1.opExtrude","SWEPT_FACE",FACE,{"disambiguationData":[OSD([subQ41])]})])],"derivedFrom":makeQuery(id+"F1.opExtrude","CAP_FACE",FACE,{"disambiguationData":[OSD([sQuery(id+"F0.wireOp",EDGE,"E0.top"),sQuery(id+"F0.wireOp",EDGE,"E0.left"),sQuery(id+"F0.wireOp",EDGE,"E1.bottom"),subQ45,sQuery(id+"F0.wireOp",EDGE,"E1.left"),sQuery(id+"F0.wireOp",EDGE,"E1.right"),subQ41,subQ40,subQ43,sQuery(id+"F0.wireOp",EDGE,"E5"),subQ8,subQ47,subQ18,sQuery(id+"F0.wireOp",EDGE,"E7.top"),subQ12,subQ14,sQuery(id+"F0.wireOp",EDGE,"E8.top"),sQuery(id+"F0.wireOp",EDGE,"E9.trimOffspring"),sQuery(id+"F0.wireOp",EDGE,"E10"),sQuery(id+"F0.wireOp",EDGE,"E11"),sQuery(id+"F0.wireOp",EDGE,"E12"),sQuery(id+"F0.wireOp",EDGE,"E14"),subQ6,subQ38,subQ37,subQ20,sQuery(id+"F0.wireOp",EDGE,"E27"),subQ4,subQ2,subQ0,subQ39,subQ42,subQ46,sQuery(id+"F0.wireOp",EDGE,"E38"),sQuery(id+"F0.wireOp",EDGE,"E39"),sQuery(id+"F0.wireOp",EDGE,"E40"),sQuery(id+"F0.wireOp",EDGE,"E41"),subQ10,subQ16,subQ22,subQ24,subQ27,subQ26,subQ29,subQ31,subQ33,sQuery(id+"F0.wireOp",EDGE,"E54.bottom"),subQ48,sQuery(id+"F0.wireOp",EDGE,"E54.left"),subQ49,subQ50,sQuery(id+"F0.wireOp",EDGE,"E60.MirrorCS"),sQuery(id+"F0.wireOp",EDGE,"E61.MirrorCS"),subQ51])],"isStart":false})})})]});}
            var Q8;
            Q8=makeQuery(id+"F1.opExtrude","CAP_EDGE",EDGE,{"disambiguationData":[OSD([sQuery(id+"F0.wireOp",EDGE,"E7.left")])],"isStart":false});
            var Q9;
            Q9=makeQuery(id+"F1.opExtrude","CAP_EDGE",EDGE,{"disambiguationData":[OSD([sQuery(id+"F0.wireOp",EDGE,"E9.trimOffspring")])],"isStart":false});
            var Q10;
            Q10=makeQuery(id+"F18.opChamfer","BLEND_EDGE",EDGE,{"blendedFrom":[makeQuery(id+"F11.opExtrude","CAP_EDGE",EDGE,{"disambiguationData":[OSD([sQuery(id+"F10.wireOp",EDGE,"E88.left")])],"isStart":false}),makeQuery(id+"F17.boolean.opBoolean","MERGE",FACE,{"derivedFrom":[makeQuery(id+"F11.boolean.opBoolean","MERGE",FACE,{"derivedFrom":[makeQuery(id+"F1.opExtrude","SWEPT_FACE",FACE,{"disambiguationData":[OSD([sQuery(id+"F0.wireOp",EDGE,"E7.top")])]}),makeQuery(id+"F11.opExtrude","SWEPT_FACE",FACE,{"disambiguationData":[OSD([sQuery(id+"F10.wireOp",EDGE,"E88.bottom")])]})]})],"fromTools":[makeQuery(id+"F17.opExtrude","SWEPT_FACE",FACE,{"disambiguationData":[OSD([sQuery(id+"F16.wireOp",EDGE,"E93")])]})]})],"blendedInto":[makeQuery(id+"F17.boolean.opBoolean","MERGE",FACE,{"derivedFrom":[makeQuery(id+"F11.boolean.opBoolean","MERGE",FACE,{"derivedFrom":[makeQuery(id+"F1.opExtrude","SWEPT_FACE",FACE,{"disambiguationData":[OSD([sQuery(id+"F0.wireOp",EDGE,"E7.top")])]}),makeQuery(id+"F11.opExtrude","SWEPT_FACE",FACE,{"disambiguationData":[OSD([sQuery(id+"F10.wireOp",EDGE,"E88.bottom")])]})]})],"fromTools":[makeQuery(id+"F17.opExtrude","SWEPT_FACE",FACE,{"disambiguationData":[OSD([sQuery(id+"F16.wireOp",EDGE,"E93")])]})]})]});
            var Q11;
            Q11=makeQuery(id+"F1.opExtrude","CAP_EDGE",EDGE,{"disambiguationData":[OSD([sQuery(id+"F0.wireOp",EDGE,"E1.bottom")])],"isStart":false});
            var Q12;
            {var subQ0=sQuery(id+"F0.wireOp",EDGE,"E41");var subQ2=sQuery(id+"F0.wireOp",EDGE,"E38");var subQ4=sQuery(id+"F0.wireOp",EDGE,"E1.right");var subQ6=sQuery(id+"F0.wireOp",EDGE,"E61.MirrorCS");var subQ8=sQuery(id+"F0.wireOp",EDGE,"E0.top");var subQ9=makeQuery(id+"F1.opExtrude","SWEPT_FACE",FACE,{"disambiguationData":[OSD([subQ8])]});var subQ10=sQuery(id+"F0.wireOp",EDGE,"E54.bottom");var subQ12=sQuery(id+"F0.wireOp",EDGE,"E39");var subQ14=sQuery(id+"F0.wireOp",EDGE,"E5");var subQ15=sQuery(id+"F0.wireOp",EDGE,"E0.left");var subQ17=sQuery(id+"F0.wireOp",EDGE,"E54.left");var subQ19=sQuery(id+"F0.wireOp",EDGE,"E40");var subQ21=sQuery(id+"F0.wireOp",EDGE,"E1.bottom");var subQ23=sQuery(id+"F0.wireOp",EDGE,"E1.left");var subQ25=sQuery(id+"F0.wireOp",EDGE,"E60.MirrorCS");var subQ27=sQuery(id+"F0.wireOp",EDGE,"E14");var subQ28=sQuery(id+"F0.wireOp",EDGE,"E1.top");Q12=makeQuery(id+"F27.opFillet","BLEND_EDGE",EDGE,{"blendedFrom":[makeQuery(id+"F1.opExtrude","SWEPT_EDGE",EDGE,{"disambiguationData":[OSD([subQ23,subQ10])]}),makeQuery(id+"F13.boolean.opBoolean","SPLIT",FACE,{"disambiguationData":[TD([subQ9])],"derivedFrom":makeQuery(id+"F3.boolean.opBoolean","SPLIT",FACE,{"disambiguationData":[TD([subQ9])],"derivedFrom":makeQuery(id+"F1.opExtrude","CAP_FACE",FACE,{"disambiguationData":[OSD([subQ8,subQ15,subQ21,subQ28,subQ23,subQ4,sQuery(id+"F0.wireOp",EDGE,"E2.top"),sQuery(id+"F0.wireOp",EDGE,"E3.trimOffspring"),sQuery(id+"F0.wireOp",EDGE,"E4"),subQ14,sQuery(id+"F0.wireOp",EDGE,"E6.top"),sQuery(id+"F0.wireOp",EDGE,"E6.left"),sQuery(id+"F0.wireOp",EDGE,"E7.bottom"),sQuery(id+"F0.wireOp",EDGE,"E7.top"),sQuery(id+"F0.wireOp",EDGE,"E7.left"),sQuery(id+"F0.wireOp",EDGE,"E7.right"),sQuery(id+"F0.wireOp",EDGE,"E8.top"),sQuery(id+"F0.wireOp",EDGE,"E9.trimOffspring"),sQuery(id+"F0.wireOp",EDGE,"E10"),sQuery(id+"F0.wireOp",EDGE,"E11"),sQuery(id+"F0.wireOp",EDGE,"E12"),subQ27,sQuery(id+"F0.wireOp",EDGE,"E15"),sQuery(id+"F0.wireOp",EDGE,"E16"),sQuery(id+"F0.wireOp",EDGE,"E18"),sQuery(id+"F0.wireOp",EDGE,"E25"),sQuery(id+"F0.wireOp",EDGE,"E27"),sQuery(id+"F0.wireOp",EDGE,"E29"),sQuery(id+"F0.wireOp",EDGE,"E30"),sQuery(id+"F0.wireOp",EDGE,"E31"),sQuery(id+"F0.wireOp",EDGE,"E35"),sQuery(id+"F0.wireOp",EDGE,"E36"),sQuery(id+"F0.wireOp",EDGE,"E37"),subQ2,subQ12,subQ19,subQ0,sQuery(id+"F0.wireOp",EDGE,"E42.bottom"),sQuery(id+"F0.wireOp",EDGE,"E42.left"),sQuery(id+"F0.wireOp",EDGE,"E42.right"),sQuery(id+"F0.wireOp",EDGE,"E45"),sQuery(id+"F0.wireOp",EDGE,"E46"),sQuery(id+"F0.wireOp",EDGE,"E47.MirrorCS"),sQuery(id+"F0.wireOp",EDGE,"E48.MirrorCS"),sQuery(id+"F0.wireOp",EDGE,"E51.trimOffspring"),sQuery(id+"F0.wireOp",EDGE,"E52.trimOffspring"),subQ10,sQuery(id+"F0.wireOp",EDGE,"E54.top"),subQ17,sQuery(id+"F0.wireOp",EDGE,"E57"),sQuery(id+"F0.wireOp",EDGE,"E58"),subQ25,subQ6,sQuery(id+"F0.wireOp",EDGE,"E62.trimOffspring")])],"isStart":false})})})],"blendedInto":[makeQuery(id+"F13.boolean.opBoolean","SPLIT",FACE,{"disambiguationData":[TD([subQ9])],"derivedFrom":makeQuery(id+"F3.boolean.opBoolean","SPLIT",FACE,{"disambiguationData":[TD([subQ9])],"derivedFrom":makeQuery(id+"F1.opExtrude","CAP_FACE",FACE,{"disambiguationData":[OSD([subQ8,subQ15,subQ21,subQ28,subQ23,subQ4,sQuery(id+"F0.wireOp",EDGE,"E2.top"),sQuery(id+"F0.wireOp",EDGE,"E3.trimOffspring"),sQuery(id+"F0.wireOp",EDGE,"E4"),subQ14,sQuery(id+"F0.wireOp",EDGE,"E6.top"),sQuery(id+"F0.wireOp",EDGE,"E6.left"),sQuery(id+"F0.wireOp",EDGE,"E7.bottom"),sQuery(id+"F0.wireOp",EDGE,"E7.top"),sQuery(id+"F0.wireOp",EDGE,"E7.left"),sQuery(id+"F0.wireOp",EDGE,"E7.right"),sQuery(id+"F0.wireOp",EDGE,"E8.top"),sQuery(id+"F0.wireOp",EDGE,"E9.trimOffspring"),sQuery(id+"F0.wireOp",EDGE,"E10"),sQuery(id+"F0.wireOp",EDGE,"E11"),sQuery(id+"F0.wireOp",EDGE,"E12"),subQ27,sQuery(id+"F0.wireOp",EDGE,"E15"),sQuery(id+"F0.wireOp",EDGE,"E16"),sQuery(id+"F0.wireOp",EDGE,"E18"),sQuery(id+"F0.wireOp",EDGE,"E25"),sQuery(id+"F0.wireOp",EDGE,"E27"),sQuery(id+"F0.wireOp",EDGE,"E29"),sQuery(id+"F0.wireOp",EDGE,"E30"),sQuery(id+"F0.wireOp",EDGE,"E31"),sQuery(id+"F0.wireOp",EDGE,"E35"),sQuery(id+"F0.wireOp",EDGE,"E36"),sQuery(id+"F0.wireOp",EDGE,"E37"),subQ2,subQ12,subQ19,subQ0,sQuery(id+"F0.wireOp",EDGE,"E42.bottom"),sQuery(id+"F0.wireOp",EDGE,"E42.left"),sQuery(id+"F0.wireOp",EDGE,"E42.right"),sQuery(id+"F0.wireOp",EDGE,"E45"),sQuery(id+"F0.wireOp",EDGE,"E46"),sQuery(id+"F0.wireOp",EDGE,"E47.MirrorCS"),sQuery(id+"F0.wireOp",EDGE,"E48.MirrorCS"),sQuery(id+"F0.wireOp",EDGE,"E51.trimOffspring"),sQuery(id+"F0.wireOp",EDGE,"E52.trimOffspring"),subQ10,sQuery(id+"F0.wireOp",EDGE,"E54.top"),subQ17,sQuery(id+"F0.wireOp",EDGE,"E57"),sQuery(id+"F0.wireOp",EDGE,"E58"),subQ25,subQ6,sQuery(id+"F0.wireOp",EDGE,"E62.trimOffspring")])],"isStart":false})})})]});}
            var Q13;
            Q13=makeQuery(id+"F1.opExtrude","CAP_EDGE",EDGE,{"disambiguationData":[OSD([sQuery(id+"F0.wireOp",EDGE,"E54.left")])],"isStart":false});
            var Q14;
            Q14=makeQuery(id+"F1.opExtrude","CAP_EDGE",EDGE,{"disambiguationData":[OSD([sQuery(id+"F0.wireOp",EDGE,"E62.trimOffspring")])],"isStart":false});
            var Q15;
            {var subQ0=sQuery(id+"F0.wireOp",EDGE,"E57");var subQ2=sQuery(id+"F0.wireOp",EDGE,"E54.top");var subQ4=sQuery(id+"F0.wireOp",EDGE,"E37");var subQ6=sQuery(id+"F0.wireOp",EDGE,"E4");var subQ8=sQuery(id+"F0.wireOp",EDGE,"E15");var subQ10=sQuery(id+"F0.wireOp",EDGE,"E35");var subQ12=sQuery(id+"F0.wireOp",EDGE,"E3.trimOffspring");var subQ15=sQuery(id+"F0.wireOp",EDGE,"E1.top");var subQ16=makeQuery(id+"F1.opExtrude","SWEPT_FACE",FACE,{"disambiguationData":[OSD([subQ15])]});var subQ17=sQuery(id+"F0.wireOp",EDGE,"E58");var subQ19=sQuery(id+"F0.wireOp",EDGE,"E2.top");var subQ20=makeQuery(id+"F1.opExtrude","SWEPT_FACE",FACE,{"disambiguationData":[OSD([subQ19])]});var subQ21=sQuery(id+"F0.wireOp",EDGE,"E62.trimOffspring");var subQ23=sQuery(id+"F0.wireOp",EDGE,"E36");var subQ25=sQuery(id+"F0.wireOp",EDGE,"E30");var subQ26=sQuery(id+"F0.wireOp",EDGE,"E29");var subQ29=sQuery(id+"F0.wireOp",EDGE,"E25");var subQ30=sQuery(id+"F0.wireOp",EDGE,"E18");var subQ31=sQuery(id+"F0.wireOp",EDGE,"E16");var subQ32=sQuery(id+"F0.wireOp",EDGE,"E31");var subQ33=sQuery(id+"F0.wireOp",EDGE,"E42.bottom");var subQ34=sQuery(id+"F0.wireOp",EDGE,"E7.left");var subQ35=sQuery(id+"F0.wireOp",EDGE,"E6.top");var subQ36=sQuery(id+"F0.wireOp",EDGE,"E6.left");var subQ37=sQuery(id+"F0.wireOp",EDGE,"E7.bottom");var subQ38=sQuery(id+"F0.wireOp",EDGE,"E42.left");var subQ39=sQuery(id+"F0.wireOp",EDGE,"E7.right");var subQ40=sQuery(id+"F0.wireOp",EDGE,"E42.right");var subQ41=sQuery(id+"F0.wireOp",EDGE,"E45");var subQ42=sQuery(id+"F0.wireOp",EDGE,"E47.MirrorCS");var subQ43=sQuery(id+"F0.wireOp",EDGE,"E46");var subQ44=sQuery(id+"F0.wireOp",EDGE,"E48.MirrorCS");var subQ45=sQuery(id+"F0.wireOp",EDGE,"E51.trimOffspring");var subQ46=sQuery(id+"F0.wireOp",EDGE,"E52.trimOffspring");Q15=makeQuery(id+"F27.opFillet","BLEND_EDGE",EDGE,{"blendedFrom":[makeQuery(id+"F1.opExtrude","SWEPT_EDGE",EDGE,{"disambiguationData":[OSD([subQ12,subQ2])]}),makeQuery(id+"F20.boolean.opBoolean","SPLIT",FACE,{"disambiguationData":[TD([subQ16])],"derivedFrom":makeQuery(id+"F3.boolean.opBoolean","SPLIT",FACE,{"disambiguationData":[TD([subQ20])],"derivedFrom":makeQuery(id+"F1.opExtrude","CAP_FACE",FACE,{"disambiguationData":[OSD([sQuery(id+"F0.wireOp",EDGE,"E0.top"),sQuery(id+"F0.wireOp",EDGE,"E0.left"),sQuery(id+"F0.wireOp",EDGE,"E1.bottom"),subQ15,sQuery(id+"F0.wireOp",EDGE,"E1.left"),sQuery(id+"F0.wireOp",EDGE,"E1.right"),subQ19,subQ12,subQ6,sQuery(id+"F0.wireOp",EDGE,"E5"),subQ35,subQ36,subQ37,sQuery(id+"F0.wireOp",EDGE,"E7.top"),subQ34,subQ39,sQuery(id+"F0.wireOp",EDGE,"E8.top"),sQuery(id+"F0.wireOp",EDGE,"E9.trimOffspring"),sQuery(id+"F0.wireOp",EDGE,"E10"),sQuery(id+"F0.wireOp",EDGE,"E11"),sQuery(id+"F0.wireOp",EDGE,"E12"),sQuery(id+"F0.wireOp",EDGE,"E14"),subQ8,subQ31,subQ30,subQ29,sQuery(id+"F0.wireOp",EDGE,"E27"),subQ26,subQ25,subQ32,subQ10,subQ23,subQ4,sQuery(id+"F0.wireOp",EDGE,"E38"),sQuery(id+"F0.wireOp",EDGE,"E39"),sQuery(id+"F0.wireOp",EDGE,"E40"),sQuery(id+"F0.wireOp",EDGE,"E41"),subQ33,subQ38,subQ40,subQ41,subQ43,subQ42,subQ44,subQ45,subQ46,sQuery(id+"F0.wireOp",EDGE,"E54.bottom"),subQ2,sQuery(id+"F0.wireOp",EDGE,"E54.left"),subQ0,subQ17,sQuery(id+"F0.wireOp",EDGE,"E60.MirrorCS"),sQuery(id+"F0.wireOp",EDGE,"E61.MirrorCS"),subQ21])],"isStart":false})})})],"blendedInto":[makeQuery(id+"F20.boolean.opBoolean","SPLIT",FACE,{"disambiguationData":[TD([subQ16])],"derivedFrom":makeQuery(id+"F3.boolean.opBoolean","SPLIT",FACE,{"disambiguationData":[TD([subQ20])],"derivedFrom":makeQuery(id+"F1.opExtrude","CAP_FACE",FACE,{"disambiguationData":[OSD([sQuery(id+"F0.wireOp",EDGE,"E0.top"),sQuery(id+"F0.wireOp",EDGE,"E0.left"),sQuery(id+"F0.wireOp",EDGE,"E1.bottom"),subQ15,sQuery(id+"F0.wireOp",EDGE,"E1.left"),sQuery(id+"F0.wireOp",EDGE,"E1.right"),subQ19,subQ12,subQ6,sQuery(id+"F0.wireOp",EDGE,"E5"),subQ35,subQ36,subQ37,sQuery(id+"F0.wireOp",EDGE,"E7.top"),subQ34,subQ39,sQuery(id+"F0.wireOp",EDGE,"E8.top"),sQuery(id+"F0.wireOp",EDGE,"E9.trimOffspring"),sQuery(id+"F0.wireOp",EDGE,"E10"),sQuery(id+"F0.wireOp",EDGE,"E11"),sQuery(id+"F0.wireOp",EDGE,"E12"),sQuery(id+"F0.wireOp",EDGE,"E14"),subQ8,subQ31,subQ30,subQ29,sQuery(id+"F0.wireOp",EDGE,"E27"),subQ26,subQ25,subQ32,subQ10,subQ23,subQ4,sQuery(id+"F0.wireOp",EDGE,"E38"),sQuery(id+"F0.wireOp",EDGE,"E39"),sQuery(id+"F0.wireOp",EDGE,"E40"),sQuery(id+"F0.wireOp",EDGE,"E41"),subQ33,subQ38,subQ40,subQ41,subQ43,subQ42,subQ44,subQ45,subQ46,sQuery(id+"F0.wireOp",EDGE,"E54.bottom"),subQ2,sQuery(id+"F0.wireOp",EDGE,"E54.left"),subQ0,subQ17,sQuery(id+"F0.wireOp",EDGE,"E60.MirrorCS"),sQuery(id+"F0.wireOp",EDGE,"E61.MirrorCS"),subQ21])],"isStart":false})})})]});}
            var Q16;
            {var subQ0=sQuery(id+"F0.wireOp",EDGE,"E3.trimOffspring");var subQ1=sQuery(id+"F0.wireOp",EDGE,"E16");var subQ2=sQuery(id+"F0.wireOp",EDGE,"E1.top");var subQ3=makeQuery(id+"F1.opExtrude","SWEPT_FACE",FACE,{"disambiguationData":[OSD([subQ2])]});var subQ4=makeQuery(id+"F1.opExtrude","CAP_FACE",FACE,{"disambiguationData":[OSD([sQuery(id+"F0.wireOp",EDGE,"E0.top"),sQuery(id+"F0.wireOp",EDGE,"E0.left"),sQuery(id+"F0.wireOp",EDGE,"E1.bottom"),subQ2,sQuery(id+"F0.wireOp",EDGE,"E1.left"),sQuery(id+"F0.wireOp",EDGE,"E1.right"),sQuery(id+"F0.wireOp",EDGE,"E2.top"),subQ0,sQuery(id+"F0.wireOp",EDGE,"E4"),sQuery(id+"F0.wireOp",EDGE,"E5"),sQuery(id+"F0.wireOp",EDGE,"E6.top"),sQuery(id+"F0.wireOp",EDGE,"E6.left"),sQuery(id+"F0.wireOp",EDGE,"E7.bottom"),sQuery(id+"F0.wireOp",EDGE,"E7.top"),sQuery(id+"F0.wireOp",EDGE,"E7.left"),sQuery(id+"F0.wireOp",EDGE,"E7.right"),sQuery(id+"F0.wireOp",EDGE,"E8.top"),sQuery(id+"F0.wireOp",EDGE,"E9.trimOffspring"),sQuery(id+"F0.wireOp",EDGE,"E10"),sQuery(id+"F0.wireOp",EDGE,"E11"),sQuery(id+"F0.wireOp",EDGE,"E12"),sQuery(id+"F0.wireOp",EDGE,"E14"),sQuery(id+"F0.wireOp",EDGE,"E15"),subQ1,sQuery(id+"F0.wireOp",EDGE,"E18"),sQuery(id+"F0.wireOp",EDGE,"E25"),sQuery(id+"F0.wireOp",EDGE,"E27"),sQuery(id+"F0.wireOp",EDGE,"E29"),sQuery(id+"F0.wireOp",EDGE,"E30"),sQuery(id+"F0.wireOp",EDGE,"E31"),sQuery(id+"F0.wireOp",EDGE,"E35"),sQuery(id+"F0.wireOp",EDGE,"E36"),sQuery(id+"F0.wireOp",EDGE,"E37"),sQuery(id+"F0.wireOp",EDGE,"E38"),sQuery(id+"F0.wireOp",EDGE,"E39"),sQuery(id+"F0.wireOp",EDGE,"E40"),sQuery(id+"F0.wireOp",EDGE,"E41"),sQuery(id+"F0.wireOp",EDGE,"E42.bottom"),sQuery(id+"F0.wireOp",EDGE,"E42.left"),sQuery(id+"F0.wireOp",EDGE,"E42.right"),sQuery(id+"F0.wireOp",EDGE,"E45"),sQuery(id+"F0.wireOp",EDGE,"E46"),sQuery(id+"F0.wireOp",EDGE,"E47.MirrorCS"),sQuery(id+"F0.wireOp",EDGE,"E48.MirrorCS"),sQuery(id+"F0.wireOp",EDGE,"E51.trimOffspring"),sQuery(id+"F0.wireOp",EDGE,"E52.trimOffspring"),sQuery(id+"F0.wireOp",EDGE,"E54.bottom"),sQuery(id+"F0.wireOp",EDGE,"E54.top"),sQuery(id+"F0.wireOp",EDGE,"E54.left"),sQuery(id+"F0.wireOp",EDGE,"E57"),sQuery(id+"F0.wireOp",EDGE,"E58"),sQuery(id+"F0.wireOp",EDGE,"E60.MirrorCS"),sQuery(id+"F0.wireOp",EDGE,"E61.MirrorCS"),sQuery(id+"F0.wireOp",EDGE,"E62.trimOffspring")])],"isStart":false});Q16=makeQuery(id+"F3.boolean.opBoolean","SPLIT",EDGE,{"disambiguationData":[topologyDisambiguationEdgeConnected([subQ4,subQ3]),TD([makeQuery(id+"F1.opExtrude","SWEPT_FACE",FACE,{"disambiguationData":[OSD([subQ0])]})])],"derivedFrom":makeQuery(id+"F1.opExtrude","CAP_EDGE",EDGE,{"disambiguationData":[OSD([subQ2])],"isStart":false})});}
            var Q17;
            Q17=makeQuery(id+"F20.opExtrude","CAP_EDGE",EDGE,{"disambiguationData":[OSD([sQuery(id+"F19.wireOp",EDGE,"E95"),sQuery(id+"F19.wireOp",EDGE,"E97")])],"isStart":false});
            var Q18;
            Q18=makeQuery(id+"F1.opExtrude","CAP_EDGE",EDGE,{"disambiguationData":[OSD([sQuery(id+"F0.wireOp",EDGE,"E6.top")])],"isStart":false});
            var Q19;
            Q19=makeQuery(id+"F1.opExtrude","CAP_EDGE",EDGE,{"disambiguationData":[OSD([sQuery(id+"F0.wireOp",EDGE,"E1.right")])],"isStart":false});
            var Q20;
            Q20=makeQuery(id+"F20.opExtrude","CAP_EDGE",EDGE,{"disambiguationData":[OSD([sQuery(id+"F19.wireOp",EDGE,"E98")])],"isStart":false});
            var Q21;
            Q21=makeQuery(id+"F20.opExtrude","CAP_EDGE",EDGE,{"disambiguationData":[OSD([sQuery(id+"F19.wireOp",EDGE,"E96")])],"isStart":false});
            var Q22;
            Q22=makeQuery(id+"F17.boolean.opBoolean","COPY",EDGE,{"derivedFrom":makeQuery(id+"F17.opExtrude","SWEPT_EDGE",EDGE,{"disambiguationData":[OSD([sQuery(id+"F16.wireOp",EDGE,"E91"),sQuery(id+"F16.wireOp",EDGE,"E92")])]})});
            var Q23;
            {var subQ0=sQuery(id+"F0.wireOp",EDGE,"E57");var subQ2=sQuery(id+"F0.wireOp",EDGE,"E54.top");var subQ4=sQuery(id+"F0.wireOp",EDGE,"E37");var subQ6=sQuery(id+"F0.wireOp",EDGE,"E4");var subQ8=sQuery(id+"F0.wireOp",EDGE,"E15");var subQ10=sQuery(id+"F0.wireOp",EDGE,"E35");var subQ12=sQuery(id+"F0.wireOp",EDGE,"E3.trimOffspring");var subQ15=sQuery(id+"F0.wireOp",EDGE,"E1.top");var subQ16=makeQuery(id+"F1.opExtrude","SWEPT_FACE",FACE,{"disambiguationData":[OSD([subQ15])]});var subQ17=sQuery(id+"F0.wireOp",EDGE,"E58");var subQ19=sQuery(id+"F0.wireOp",EDGE,"E2.top");var subQ20=makeQuery(id+"F1.opExtrude","SWEPT_FACE",FACE,{"disambiguationData":[OSD([subQ19])]});var subQ21=sQuery(id+"F0.wireOp",EDGE,"E62.trimOffspring");var subQ23=sQuery(id+"F0.wireOp",EDGE,"E36");var subQ25=sQuery(id+"F0.wireOp",EDGE,"E30");var subQ26=sQuery(id+"F0.wireOp",EDGE,"E29");var subQ29=sQuery(id+"F0.wireOp",EDGE,"E25");var subQ30=sQuery(id+"F0.wireOp",EDGE,"E18");var subQ31=sQuery(id+"F0.wireOp",EDGE,"E16");var subQ32=sQuery(id+"F0.wireOp",EDGE,"E31");var subQ33=sQuery(id+"F0.wireOp",EDGE,"E42.bottom");var subQ34=sQuery(id+"F0.wireOp",EDGE,"E7.left");var subQ35=sQuery(id+"F0.wireOp",EDGE,"E6.top");var subQ36=sQuery(id+"F0.wireOp",EDGE,"E6.left");var subQ37=sQuery(id+"F0.wireOp",EDGE,"E7.bottom");var subQ38=sQuery(id+"F0.wireOp",EDGE,"E42.left");var subQ39=sQuery(id+"F0.wireOp",EDGE,"E7.right");var subQ40=sQuery(id+"F0.wireOp",EDGE,"E42.right");var subQ41=sQuery(id+"F0.wireOp",EDGE,"E45");var subQ42=sQuery(id+"F0.wireOp",EDGE,"E47.MirrorCS");var subQ43=sQuery(id+"F0.wireOp",EDGE,"E46");var subQ44=sQuery(id+"F0.wireOp",EDGE,"E48.MirrorCS");var subQ45=sQuery(id+"F0.wireOp",EDGE,"E51.trimOffspring");var subQ46=sQuery(id+"F0.wireOp",EDGE,"E52.trimOffspring");Q23=makeQuery(id+"F27.opFillet","BLEND_EDGE",EDGE,{"blendedFrom":[makeQuery(id+"F1.opExtrude","SWEPT_EDGE",EDGE,{"disambiguationData":[OSD([subQ0,subQ17])]}),makeQuery(id+"F20.boolean.opBoolean","SPLIT",FACE,{"disambiguationData":[TD([subQ16])],"derivedFrom":makeQuery(id+"F3.boolean.opBoolean","SPLIT",FACE,{"disambiguationData":[TD([subQ20])],"derivedFrom":makeQuery(id+"F1.opExtrude","CAP_FACE",FACE,{"disambiguationData":[OSD([sQuery(id+"F0.wireOp",EDGE,"E0.top"),sQuery(id+"F0.wireOp",EDGE,"E0.left"),sQuery(id+"F0.wireOp",EDGE,"E1.bottom"),subQ15,sQuery(id+"F0.wireOp",EDGE,"E1.left"),sQuery(id+"F0.wireOp",EDGE,"E1.right"),subQ19,subQ12,subQ6,sQuery(id+"F0.wireOp",EDGE,"E5"),subQ35,subQ36,subQ37,sQuery(id+"F0.wireOp",EDGE,"E7.top"),subQ34,subQ39,sQuery(id+"F0.wireOp",EDGE,"E8.top"),sQuery(id+"F0.wireOp",EDGE,"E9.trimOffspring"),sQuery(id+"F0.wireOp",EDGE,"E10"),sQuery(id+"F0.wireOp",EDGE,"E11"),sQuery(id+"F0.wireOp",EDGE,"E12"),sQuery(id+"F0.wireOp",EDGE,"E14"),subQ8,subQ31,subQ30,subQ29,sQuery(id+"F0.wireOp",EDGE,"E27"),subQ26,subQ25,subQ32,subQ10,subQ23,subQ4,sQuery(id+"F0.wireOp",EDGE,"E38"),sQuery(id+"F0.wireOp",EDGE,"E39"),sQuery(id+"F0.wireOp",EDGE,"E40"),sQuery(id+"F0.wireOp",EDGE,"E41"),subQ33,subQ38,subQ40,subQ41,subQ43,subQ42,subQ44,subQ45,subQ46,sQuery(id+"F0.wireOp",EDGE,"E54.bottom"),subQ2,sQuery(id+"F0.wireOp",EDGE,"E54.left"),subQ0,subQ17,sQuery(id+"F0.wireOp",EDGE,"E60.MirrorCS"),sQuery(id+"F0.wireOp",EDGE,"E61.MirrorCS"),subQ21])],"isStart":false})})})],"blendedInto":[makeQuery(id+"F20.boolean.opBoolean","SPLIT",FACE,{"disambiguationData":[TD([subQ16])],"derivedFrom":makeQuery(id+"F3.boolean.opBoolean","SPLIT",FACE,{"disambiguationData":[TD([subQ20])],"derivedFrom":makeQuery(id+"F1.opExtrude","CAP_FACE",FACE,{"disambiguationData":[OSD([sQuery(id+"F0.wireOp",EDGE,"E0.top"),sQuery(id+"F0.wireOp",EDGE,"E0.left"),sQuery(id+"F0.wireOp",EDGE,"E1.bottom"),subQ15,sQuery(id+"F0.wireOp",EDGE,"E1.left"),sQuery(id+"F0.wireOp",EDGE,"E1.right"),subQ19,subQ12,subQ6,sQuery(id+"F0.wireOp",EDGE,"E5"),subQ35,subQ36,subQ37,sQuery(id+"F0.wireOp",EDGE,"E7.top"),subQ34,subQ39,sQuery(id+"F0.wireOp",EDGE,"E8.top"),sQuery(id+"F0.wireOp",EDGE,"E9.trimOffspring"),sQuery(id+"F0.wireOp",EDGE,"E10"),sQuery(id+"F0.wireOp",EDGE,"E11"),sQuery(id+"F0.wireOp",EDGE,"E12"),sQuery(id+"F0.wireOp",EDGE,"E14"),subQ8,subQ31,subQ30,subQ29,sQuery(id+"F0.wireOp",EDGE,"E27"),subQ26,subQ25,subQ32,subQ10,subQ23,subQ4,sQuery(id+"F0.wireOp",EDGE,"E38"),sQuery(id+"F0.wireOp",EDGE,"E39"),sQuery(id+"F0.wireOp",EDGE,"E40"),sQuery(id+"F0.wireOp",EDGE,"E41"),subQ33,subQ38,subQ40,subQ41,subQ43,subQ42,subQ44,subQ45,subQ46,sQuery(id+"F0.wireOp",EDGE,"E54.bottom"),subQ2,sQuery(id+"F0.wireOp",EDGE,"E54.left"),subQ0,subQ17,sQuery(id+"F0.wireOp",EDGE,"E60.MirrorCS"),sQuery(id+"F0.wireOp",EDGE,"E61.MirrorCS"),subQ21])],"isStart":false})})})]});}
            var Q24;
            {var subQ0=sQuery(id+"F0.wireOp",EDGE,"E41");var subQ2=sQuery(id+"F0.wireOp",EDGE,"E38");var subQ4=sQuery(id+"F0.wireOp",EDGE,"E1.right");var subQ6=sQuery(id+"F0.wireOp",EDGE,"E61.MirrorCS");var subQ8=sQuery(id+"F0.wireOp",EDGE,"E0.top");var subQ9=makeQuery(id+"F1.opExtrude","SWEPT_FACE",FACE,{"disambiguationData":[OSD([subQ8])]});var subQ10=sQuery(id+"F0.wireOp",EDGE,"E54.bottom");var subQ12=sQuery(id+"F0.wireOp",EDGE,"E39");var subQ14=sQuery(id+"F0.wireOp",EDGE,"E5");var subQ15=sQuery(id+"F0.wireOp",EDGE,"E0.left");var subQ17=sQuery(id+"F0.wireOp",EDGE,"E54.left");var subQ19=sQuery(id+"F0.wireOp",EDGE,"E40");var subQ21=sQuery(id+"F0.wireOp",EDGE,"E1.bottom");var subQ23=sQuery(id+"F0.wireOp",EDGE,"E1.left");var subQ25=sQuery(id+"F0.wireOp",EDGE,"E60.MirrorCS");var subQ27=sQuery(id+"F0.wireOp",EDGE,"E14");var subQ28=sQuery(id+"F0.wireOp",EDGE,"E1.top");Q24=makeQuery(id+"F27.opFillet","BLEND_EDGE",EDGE,{"blendedFrom":[makeQuery(id+"F1.opExtrude","SWEPT_EDGE",EDGE,{"disambiguationData":[OSD([subQ25,subQ6])]}),makeQuery(id+"F13.boolean.opBoolean","SPLIT",FACE,{"disambiguationData":[TD([subQ9])],"derivedFrom":makeQuery(id+"F3.boolean.opBoolean","SPLIT",FACE,{"disambiguationData":[TD([subQ9])],"derivedFrom":makeQuery(id+"F1.opExtrude","CAP_FACE",FACE,{"disambiguationData":[OSD([subQ8,subQ15,subQ21,subQ28,subQ23,subQ4,sQuery(id+"F0.wireOp",EDGE,"E2.top"),sQuery(id+"F0.wireOp",EDGE,"E3.trimOffspring"),sQuery(id+"F0.wireOp",EDGE,"E4"),subQ14,sQuery(id+"F0.wireOp",EDGE,"E6.top"),sQuery(id+"F0.wireOp",EDGE,"E6.left"),sQuery(id+"F0.wireOp",EDGE,"E7.bottom"),sQuery(id+"F0.wireOp",EDGE,"E7.top"),sQuery(id+"F0.wireOp",EDGE,"E7.left"),sQuery(id+"F0.wireOp",EDGE,"E7.right"),sQuery(id+"F0.wireOp",EDGE,"E8.top"),sQuery(id+"F0.wireOp",EDGE,"E9.trimOffspring"),sQuery(id+"F0.wireOp",EDGE,"E10"),sQuery(id+"F0.wireOp",EDGE,"E11"),sQuery(id+"F0.wireOp",EDGE,"E12"),subQ27,sQuery(id+"F0.wireOp",EDGE,"E15"),sQuery(id+"F0.wireOp",EDGE,"E16"),sQuery(id+"F0.wireOp",EDGE,"E18"),sQuery(id+"F0.wireOp",EDGE,"E25"),sQuery(id+"F0.wireOp",EDGE,"E27"),sQuery(id+"F0.wireOp",EDGE,"E29"),sQuery(id+"F0.wireOp",EDGE,"E30"),sQuery(id+"F0.wireOp",EDGE,"E31"),sQuery(id+"F0.wireOp",EDGE,"E35"),sQuery(id+"F0.wireOp",EDGE,"E36"),sQuery(id+"F0.wireOp",EDGE,"E37"),subQ2,subQ12,subQ19,subQ0,sQuery(id+"F0.wireOp",EDGE,"E42.bottom"),sQuery(id+"F0.wireOp",EDGE,"E42.left"),sQuery(id+"F0.wireOp",EDGE,"E42.right"),sQuery(id+"F0.wireOp",EDGE,"E45"),sQuery(id+"F0.wireOp",EDGE,"E46"),sQuery(id+"F0.wireOp",EDGE,"E47.MirrorCS"),sQuery(id+"F0.wireOp",EDGE,"E48.MirrorCS"),sQuery(id+"F0.wireOp",EDGE,"E51.trimOffspring"),sQuery(id+"F0.wireOp",EDGE,"E52.trimOffspring"),subQ10,sQuery(id+"F0.wireOp",EDGE,"E54.top"),subQ17,sQuery(id+"F0.wireOp",EDGE,"E57"),sQuery(id+"F0.wireOp",EDGE,"E58"),subQ25,subQ6,sQuery(id+"F0.wireOp",EDGE,"E62.trimOffspring")])],"isStart":false})})})],"blendedInto":[makeQuery(id+"F13.boolean.opBoolean","SPLIT",FACE,{"disambiguationData":[TD([subQ9])],"derivedFrom":makeQuery(id+"F3.boolean.opBoolean","SPLIT",FACE,{"disambiguationData":[TD([subQ9])],"derivedFrom":makeQuery(id+"F1.opExtrude","CAP_FACE",FACE,{"disambiguationData":[OSD([subQ8,subQ15,subQ21,subQ28,subQ23,subQ4,sQuery(id+"F0.wireOp",EDGE,"E2.top"),sQuery(id+"F0.wireOp",EDGE,"E3.trimOffspring"),sQuery(id+"F0.wireOp",EDGE,"E4"),subQ14,sQuery(id+"F0.wireOp",EDGE,"E6.top"),sQuery(id+"F0.wireOp",EDGE,"E6.left"),sQuery(id+"F0.wireOp",EDGE,"E7.bottom"),sQuery(id+"F0.wireOp",EDGE,"E7.top"),sQuery(id+"F0.wireOp",EDGE,"E7.left"),sQuery(id+"F0.wireOp",EDGE,"E7.right"),sQuery(id+"F0.wireOp",EDGE,"E8.top"),sQuery(id+"F0.wireOp",EDGE,"E9.trimOffspring"),sQuery(id+"F0.wireOp",EDGE,"E10"),sQuery(id+"F0.wireOp",EDGE,"E11"),sQuery(id+"F0.wireOp",EDGE,"E12"),subQ27,sQuery(id+"F0.wireOp",EDGE,"E15"),sQuery(id+"F0.wireOp",EDGE,"E16"),sQuery(id+"F0.wireOp",EDGE,"E18"),sQuery(id+"F0.wireOp",EDGE,"E25"),sQuery(id+"F0.wireOp",EDGE,"E27"),sQuery(id+"F0.wireOp",EDGE,"E29"),sQuery(id+"F0.wireOp",EDGE,"E30"),sQuery(id+"F0.wireOp",EDGE,"E31"),sQuery(id+"F0.wireOp",EDGE,"E35"),sQuery(id+"F0.wireOp",EDGE,"E36"),sQuery(id+"F0.wireOp",EDGE,"E37"),subQ2,subQ12,subQ19,subQ0,sQuery(id+"F0.wireOp",EDGE,"E42.bottom"),sQuery(id+"F0.wireOp",EDGE,"E42.left"),sQuery(id+"F0.wireOp",EDGE,"E42.right"),sQuery(id+"F0.wireOp",EDGE,"E45"),sQuery(id+"F0.wireOp",EDGE,"E46"),sQuery(id+"F0.wireOp",EDGE,"E47.MirrorCS"),sQuery(id+"F0.wireOp",EDGE,"E48.MirrorCS"),sQuery(id+"F0.wireOp",EDGE,"E51.trimOffspring"),sQuery(id+"F0.wireOp",EDGE,"E52.trimOffspring"),subQ10,sQuery(id+"F0.wireOp",EDGE,"E54.top"),subQ17,sQuery(id+"F0.wireOp",EDGE,"E57"),sQuery(id+"F0.wireOp",EDGE,"E58"),subQ25,subQ6,sQuery(id+"F0.wireOp",EDGE,"E62.trimOffspring")])],"isStart":false})})})]});}
            var Q25;
            Q25=makeQuery(id+"F1.opExtrude","CAP_EDGE",EDGE,{"disambiguationData":[OSD([sQuery(id+"F0.wireOp",EDGE,"E25")])],"isStart":false});
            fillet(context, id + "F28", {"entities" : qUnion([Q0, Q1, Q2, Q3, Q4, Q5, Q6, Q7, Q8, Q9, Q10, Q11, Q12, Q13, Q14, Q15, Q16, Q17, Q18, Q19, Q20, Q21, Q22, Q23, Q24, Q25]), "tangentPropagation" : true, "radius" : 1 * mm, "defaultsChanged" : false, "vertexSettings" : [], "allowEdgeOverflow" : false});
        }
    });
